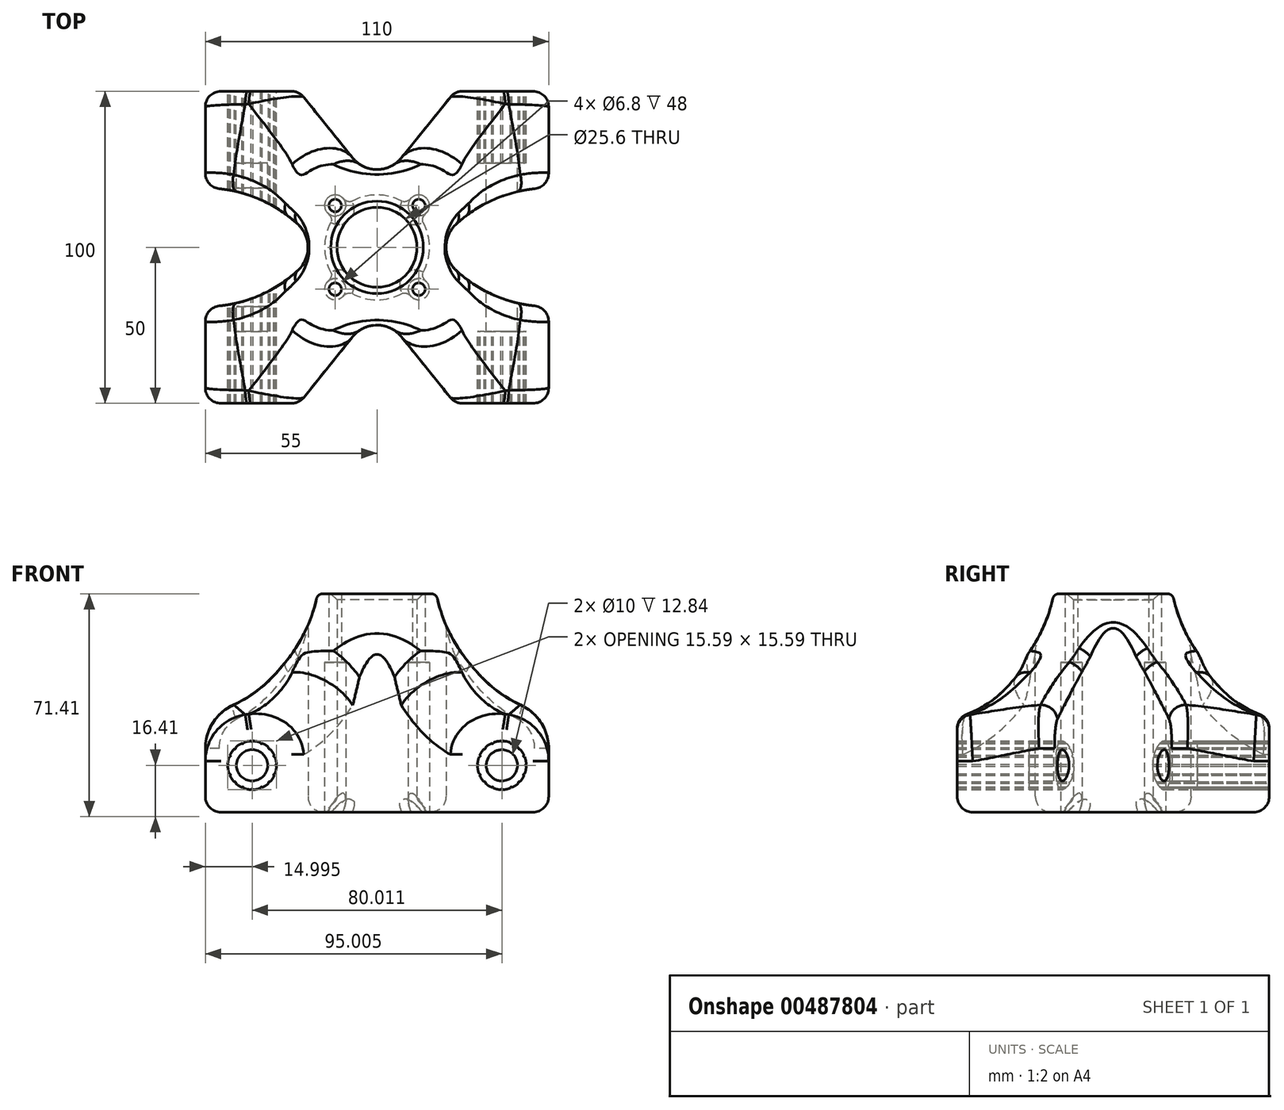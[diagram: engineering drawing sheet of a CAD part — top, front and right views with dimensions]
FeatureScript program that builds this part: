
annotation { "Feature Type Name" : "Feature", "Feature Type Description" : "" }
export const myFeature = defineFeature(function(context is Context, id is Id, definition is map)
    precondition{}
    {
        {
            var Q0;
            Q0=qCreatedBy(makeId("Top.planeOp"),FACE);
            var sketch = newSketch(context, id + "F0", { "sketchPlane" : qUnion([Q0])});
            skCircle(sketch, "E0", {"center": v(13.4, 13.4) * mm, "radius": 2 * mm});
            skCircle(sketch, "E1", {"center": v(13.4, 13.4) * mm, "radius": 3.4 * mm});
            skCircle(sketch, "E2", {"center": v(0, 0) * mm, "radius": 12.8 * mm});
            skCircle(sketch, "E3.1.0", {"center": v(-13.4, 13.4) * mm, "radius": 3.4 * mm});
            skCircle(sketch, "E3.1.1", {"center": v(-13.4, 13.4) * mm, "radius": 2 * mm});
            skCircle(sketch, "E3.2.0", {"center": v(-13.4, -13.4) * mm, "radius": 3.4 * mm});
            skCircle(sketch, "E3.2.1", {"center": v(-13.4, -13.4) * mm, "radius": 2 * mm});
            skCircle(sketch, "E3.3.0", {"center": v(13.4, -13.4) * mm, "radius": 3.4 * mm});
            skCircle(sketch, "E3.3.1", {"center": v(13.4, -13.4) * mm, "radius": 2 * mm});
            skLineSegment(sketch, "E4.bottom", {"start": v(55, -50) * mm, "end": v(-55, -50) * mm});
            skLineSegment(sketch, "E4.top", {"start": v(55, 50) * mm, "end": v(-55, 50) * mm});
            skLineSegment(sketch, "E4.left", {"start": v(55, -50) * mm, "end": v(55, 50) * mm});
            skLineSegment(sketch, "E4.right", {"start": v(-55, -50) * mm, "end": v(-55, 50) * mm});
            skLineSegment(sketch, "E5.bottom", {"start": v(25, -50) * mm, "end": v(-25, -50) * mm});
            skLineSegment(sketch, "E5.top", {"start": v(25, 50) * mm, "end": v(-25, 50) * mm});
            skLineSegment(sketch, "E5.left", {"start": v(25, -50) * mm, "end": v(25, 50) * mm});
            skLineSegment(sketch, "E5.right", {"start": v(-25, -50) * mm, "end": v(-25, 50) * mm});
            skLineSegment(sketch, "E6.bottom", {"start": v(19, -19) * mm, "end": v(-19, -19) * mm});
            skLineSegment(sketch, "E6.top", {"start": v(19, 19) * mm, "end": v(-19, 19) * mm});
            skLineSegment(sketch, "E6.left", {"start": v(19, -19) * mm, "end": v(19, 19) * mm});
            skLineSegment(sketch, "E6.right", {"start": v(-19, -19) * mm, "end": v(-19, 19) * mm});
            skLineSegment(sketch, "E7.bottom", {"start": v(55, -19) * mm, "end": v(-55, -19) * mm});
            skLineSegment(sketch, "E7.top", {"start": v(55, 19) * mm, "end": v(-55, 19) * mm});
            skLineSegment(sketch, "E7.left", {"start": v(55, -19) * mm, "end": v(55, 19) * mm});
            skLineSegment(sketch, "E7.right", {"start": v(-55, -19) * mm, "end": v(-55, 19) * mm});
            skLineSegment(sketch, "E8", {"start": v(0, 19) * mm, "end": v(-25, 50) * mm});
            skLineSegment(sketch, "E9", {"start": v(25, 50) * mm, "end": v(0, 19) * mm});
            skLineSegment(sketch, "E10", {"start": v(-25, -19) * mm, "end": v(-19, 0) * mm});
            skLineSegment(sketch, "E11", {"start": v(-19, 0) * mm, "end": v(-25, 19) * mm});
            skLineSegment(sketch, "E12", {"start": v(19, 0) * mm, "end": v(25, 19) * mm});
            skLineSegment(sketch, "E13", {"start": v(19, 0) * mm, "end": v(25, -19) * mm});
            skLineSegment(sketch, "E14", {"start": v(-25, -50) * mm, "end": v(0, -19) * mm});
            skLineSegment(sketch, "E15", {"start": v(0, -19) * mm, "end": v(25, -50) * mm});
            skSolve(sketch);
        }
        {
            var Q0;
            Q0=qCreatedBy(makeId("Front.planeOp"),FACE);
            var sketch = newSketch(context, id + "F1", { "sketchPlane" : qUnion([Q0])});
            skPoint(sketch, "E16.middle", {"position": v(40, 15) * mm});
            skPoint(sketch, "E17.center", {"position": v(40, 10) * mm});
            skCircle(sketch, "E18", {"center": v(40, 15) * mm, "radius": 7.8 * mm});
            skCircle(sketch, "E19", {"center": v(40, 22.8) * mm, "radius": 0.3 * mm});
            skCircle(sketch, "E20.1.0", {"center": v(37.02, 22.2) * mm, "radius": 0.3 * mm});
            skCircle(sketch, "E20.2.0", {"center": v(34.49, 20.52) * mm, "radius": 0.3 * mm});
            skCircle(sketch, "E20.3.0", {"center": v(32.8, 17.98) * mm, "radius": 0.3 * mm});
            skCircle(sketch, "E20.4.0", {"center": v(32.2, 15) * mm, "radius": 0.3 * mm});
            skCircle(sketch, "E20.5.0", {"center": v(32.8, 12.02) * mm, "radius": 0.3 * mm});
            skCircle(sketch, "E20.6.0", {"center": v(34.49, 9.48) * mm, "radius": 0.3 * mm});
            skCircle(sketch, "E20.7.0", {"center": v(37.02, 7.8) * mm, "radius": 0.3 * mm});
            skCircle(sketch, "E20.8.0", {"center": v(40, 7.2) * mm, "radius": 0.3 * mm});
            skCircle(sketch, "E20.9.0", {"center": v(43, 7.8) * mm, "radius": 0.3 * mm});
            skCircle(sketch, "E21.1.10.0", {"center": v(45.52, 9.48) * mm, "radius": 0.3 * mm});
            skCircle(sketch, "E21.1.11.0", {"center": v(47.21, 12.02) * mm, "radius": 0.3 * mm});
            skCircle(sketch, "E21.1.12.0", {"center": v(47.8, 15) * mm, "radius": 0.3 * mm});
            skCircle(sketch, "E21.1.13.0", {"center": v(47.21, 17.98) * mm, "radius": 0.3 * mm});
            skCircle(sketch, "E21.1.14.0", {"center": v(45.52, 20.52) * mm, "radius": 0.3 * mm});
            skCircle(sketch, "E21.1.15.0", {"center": v(43, 22.2) * mm, "radius": 0.3 * mm});
            skCircle(sketch, "E22", {"center": v(40, 15) * mm, "radius": 5 * mm});
            skPoint(sketch, "E23.MirrorP", {"position": v(-40, 15) * mm});
            skPoint(sketch, "E24.MirrorP", {"position": v(-40, 10) * mm});
            skCircle(sketch, "E25.MirrorC", {"center": v(-45.52, 9.48) * mm, "radius": 0.3 * mm});
            skCircle(sketch, "E26.MirrorC", {"center": v(-32.8, 12.02) * mm, "radius": 0.3 * mm});
            skCircle(sketch, "E27.MirrorC", {"center": v(-37.02, 22.2) * mm, "radius": 0.3 * mm});
            skCircle(sketch, "E28.MirrorC", {"center": v(-43, 7.8) * mm, "radius": 0.3 * mm});
            skCircle(sketch, "E29.MirrorC", {"center": v(-32.8, 17.98) * mm, "radius": 0.3 * mm});
            skCircle(sketch, "E30.MirrorC", {"center": v(-47.21, 12.02) * mm, "radius": 0.3 * mm});
            skCircle(sketch, "E31.MirrorC", {"center": v(-47.21, 17.98) * mm, "radius": 0.3 * mm});
            skCircle(sketch, "E32.MirrorC", {"center": v(-45.52, 20.52) * mm, "radius": 0.3 * mm});
            skCircle(sketch, "E33.MirrorC", {"center": v(-34.49, 9.48) * mm, "radius": 0.3 * mm});
            skCircle(sketch, "E34.MirrorC", {"center": v(-40, 7.2) * mm, "radius": 0.3 * mm});
            skCircle(sketch, "E35.MirrorC", {"center": v(-37.02, 7.8) * mm, "radius": 0.3 * mm});
            skCircle(sketch, "E36.MirrorC", {"center": v(-32.2, 15) * mm, "radius": 0.3 * mm});
            skCircle(sketch, "E37.MirrorC", {"center": v(-34.49, 20.52) * mm, "radius": 0.3 * mm});
            skCircle(sketch, "E38.MirrorC", {"center": v(-40, 22.8) * mm, "radius": 0.3 * mm});
            skCircle(sketch, "E39.MirrorC", {"center": v(-43, 22.2) * mm, "radius": 0.3 * mm});
            skCircle(sketch, "E40.MirrorC", {"center": v(-47.8, 15) * mm, "radius": 0.3 * mm});
            skCircle(sketch, "E41.MirrorC", {"center": v(-40, 15) * mm, "radius": 5 * mm});
            skCircle(sketch, "E42.MirrorC", {"center": v(-40, 15) * mm, "radius": 7.8 * mm});
            skLineSegment(sketch, "E43", {"start": v(-40, 15) * mm, "end": v(40, 15) * mm, "construction": true});
            skSolve(sketch);
        }
        {
            var Q0;
            Q0=makeQuery(id+"F0.imprint","IMPRINT",FACE,{"disambiguationData":[TD([[makeQuery(id+"F0.imprint","IMPRINT",EDGE,{"derivedFrom":sQuery(id+"F0.wireOp",EDGE,"E1")}),-1.0]])]});
            var Q1;
            Q1=makeQuery(id+"F0.imprint","IMPRINT",FACE,{"disambiguationData":[TD([[makeQuery(id+"F0.imprint","IMPRINT",EDGE,{"derivedFrom":sQuery(id+"F0.wireOp",EDGE,"E3.2.0")}),1.0]])]});
            var Q2;
            Q2=makeQuery(id+"F0.imprint","IMPRINT",FACE,{"disambiguationData":[TD([[makeQuery(id+"F0.imprint","IMPRINT",EDGE,{"derivedFrom":sQuery(id+"F0.wireOp",EDGE,"E3.3.0")}),1.0]])]});
            var Q3;
            Q3=makeQuery(id+"F0.imprint","IMPRINT",FACE,{"disambiguationData":[TD([[makeQuery(id+"F0.imprint","IMPRINT",EDGE,{"derivedFrom":sQuery(id+"F0.wireOp",EDGE,"E0")}),-1.0]])]});
            var Q4;
            Q4=makeQuery(id+"F0.imprint","IMPRINT",FACE,{"disambiguationData":[TD([[makeQuery(id+"F0.imprint","IMPRINT",EDGE,{"derivedFrom":sQuery(id+"F0.wireOp",EDGE,"E3.1.0")}),1.0]])]});
            extrude(context, id + "F2", {"entities" : qUnion([Q0, Q1, Q2, Q3, Q4]), "depth" : 70 * mm, "offsetDistance" : 25 * mm});
        }
        {
            var Q0;
            Q0=makeQuery(id+"F0.imprint","IMPRINT",FACE,{"disambiguationData":[TD([[makeQuery(id+"F0.imprint","IMPRINT",EDGE,{"derivedFrom":sQuery(id+"F0.wireOp",EDGE,"E3.2.0")}),1.0]])]});
            var Q1;
            Q1=makeQuery(id+"F0.imprint","IMPRINT",FACE,{"disambiguationData":[TD([[makeQuery(id+"F0.imprint","IMPRINT",EDGE,{"derivedFrom":sQuery(id+"F0.wireOp",EDGE,"E3.3.0")}),1.0]])]});
            var Q2;
            Q2=makeQuery(id+"F0.imprint","IMPRINT",FACE,{"disambiguationData":[TD([[makeQuery(id+"F0.imprint","IMPRINT",EDGE,{"derivedFrom":sQuery(id+"F0.wireOp",EDGE,"E0")}),-1.0]])]});
            var Q3;
            Q3=makeQuery(id+"F0.imprint","IMPRINT",FACE,{"disambiguationData":[TD([[makeQuery(id+"F0.imprint","IMPRINT",EDGE,{"derivedFrom":sQuery(id+"F0.wireOp",EDGE,"E3.1.0")}),1.0]])]});
            extrude(context, id + "F3", {"entities" : qUnion([Q0, Q1, Q2, Q3]), "operationType" : NewBodyOperationType.REMOVE, "depth" : (70 - 22) * mm, "offsetDistance" : 25 * mm});
        }
        {
            var Q0;
            {var subQ0=sQuery(id+"F0.wireOp",EDGE,"E14");Q0=makeQuery(id+"F0.imprint","IMPRINT",FACE,{"disambiguationData":[TD([[makeQuery(id+"F0.imprint","IMPRINT",EDGE,{"derivedFrom":subQ0}),1.0]])]});}
            var Q1;
            {var subQ3=sQuery(id+"F0.wireOp",EDGE,"E10");Q1=makeQuery(id+"F0.imprint","IMPRINT",FACE,{"disambiguationData":[TD([[makeQuery(id+"F0.imprint","IMPRINT",EDGE,{"derivedFrom":subQ3}),-1.0]])]});}
            var Q2;
            {var subQ3=sQuery(id+"F0.wireOp",EDGE,"E11");Q2=makeQuery(id+"F0.imprint","IMPRINT",FACE,{"disambiguationData":[TD([[makeQuery(id+"F0.imprint","IMPRINT",EDGE,{"derivedFrom":subQ3}),-1.0]])]});}
            var Q3;
            {var subQ0=sQuery(id+"F0.wireOp",EDGE,"E8");Q3=makeQuery(id+"F0.imprint","IMPRINT",FACE,{"disambiguationData":[TD([[makeQuery(id+"F0.imprint","IMPRINT",EDGE,{"derivedFrom":subQ0}),1.0]])]});}
            var Q4;
            {var subQ0=sQuery(id+"F0.wireOp",EDGE,"E9");Q4=makeQuery(id+"F0.imprint","IMPRINT",FACE,{"disambiguationData":[TD([[makeQuery(id+"F0.imprint","IMPRINT",EDGE,{"derivedFrom":subQ0}),1.0]])]});}
            var Q5;
            {var subQ3=sQuery(id+"F0.wireOp",EDGE,"E13");Q5=makeQuery(id+"F0.imprint","IMPRINT",FACE,{"disambiguationData":[TD([[makeQuery(id+"F0.imprint","IMPRINT",EDGE,{"derivedFrom":subQ3}),-1.0]])]});}
            var Q6;
            {var subQ3=sQuery(id+"F0.wireOp",EDGE,"E12");Q6=makeQuery(id+"F0.imprint","IMPRINT",FACE,{"disambiguationData":[TD([[makeQuery(id+"F0.imprint","IMPRINT",EDGE,{"derivedFrom":subQ3}),1.0]])]});}
            var Q7;
            {var subQ0=sQuery(id+"F0.wireOp",EDGE,"E15");Q7=makeQuery(id+"F0.imprint","IMPRINT",FACE,{"disambiguationData":[TD([[makeQuery(id+"F0.imprint","IMPRINT",EDGE,{"derivedFrom":subQ0}),1.0]])]});}
            var Q8;
            {var subQ0=sQuery(id+"F0.wireOp",EDGE,"E4.right");var subQ1=sQuery(id+"F0.wireOp",EDGE,"E4.bottom");var subQ2=makeQuery(id+"F0.imprint","INTERSECT",VERTEX,{"derivedFrom":[subQ1,subQ0]});Q8=makeQuery(id+"F0.imprint","IMPRINT",FACE,{"disambiguationData":[TD([[makeQuery(id+"F0.imprint","IMPRINT",EDGE,{"disambiguationData":[TD([[subQ2,-1.0]])],"derivedFrom":subQ0}),-1.0]])]});}
            var Q9;
            {var subQ0=sQuery(id+"F0.wireOp",EDGE,"E4.left");var subQ1=sQuery(id+"F0.wireOp",EDGE,"E4.bottom");var subQ2=makeQuery(id+"F0.imprint","INTERSECT",VERTEX,{"derivedFrom":[subQ1,subQ0]});Q9=makeQuery(id+"F0.imprint","IMPRINT",FACE,{"disambiguationData":[TD([[makeQuery(id+"F0.imprint","IMPRINT",EDGE,{"disambiguationData":[TD([[subQ2,-1.0]])],"derivedFrom":subQ0}),1.0]])]});}
            var Q10;
            {var subQ0=sQuery(id+"F0.wireOp",EDGE,"E4.left");var subQ1=sQuery(id+"F0.wireOp",EDGE,"E4.top");var subQ2=makeQuery(id+"F0.imprint","INTERSECT",VERTEX,{"derivedFrom":[subQ1,subQ0]});Q10=makeQuery(id+"F0.imprint","IMPRINT",FACE,{"disambiguationData":[TD([[makeQuery(id+"F0.imprint","IMPRINT",EDGE,{"disambiguationData":[TD([[subQ2,1.0]])],"derivedFrom":subQ0}),1.0]])]});}
            var Q11;
            {var subQ0=sQuery(id+"F0.wireOp",EDGE,"E4.right");var subQ1=sQuery(id+"F0.wireOp",EDGE,"E4.top");var subQ2=makeQuery(id+"F0.imprint","INTERSECT",VERTEX,{"derivedFrom":[subQ1,subQ0]});Q11=makeQuery(id+"F0.imprint","IMPRINT",FACE,{"disambiguationData":[TD([[makeQuery(id+"F0.imprint","IMPRINT",EDGE,{"disambiguationData":[TD([[subQ2,1.0]])],"derivedFrom":subQ0}),-1.0]])]});}
            extrude(context, id + "F4", {"entities" : qUnion([Q0, Q1, Q2, Q3, Q4, Q5, Q6, Q7, Q8, Q9, Q10, Q11]), "operationType" : NewBodyOperationType.ADD, "depth" : 30 * mm, "offsetDistance" : 25 * mm});
        }
        {
            var Q0;
            Q0=makeQuery(id+"F1.imprint","IMPRINT",FACE,{"disambiguationData":[TD([[makeQuery(id+"F1.imprint","IMPRINT",EDGE,{"derivedFrom":sQuery(id+"F1.wireOp",EDGE,"E41.MirrorC")}),-1.0]])]});
            var Q1;
            Q1=makeQuery(id+"F1.imprint","IMPRINT",FACE,{"disambiguationData":[TD([[makeQuery(id+"F1.imprint","IMPRINT",EDGE,{"derivedFrom":sQuery(id+"F1.wireOp",EDGE,"E22")}),1.0]])]});
            var Q2;
            Q2=makeQuery(id+"F1.imprint","IMPRINT",FACE,{"disambiguationData":[TD([[makeQuery(id+"F1.imprint","IMPRINT",EDGE,{"derivedFrom":sQuery(id+"F1.wireOp",EDGE,"E22")}),-1.0]])]});
            var Q3;
            Q3=makeQuery(id+"F1.imprint","IMPRINT",FACE,{"disambiguationData":[TD([[makeQuery(id+"F1.imprint","IMPRINT",EDGE,{"derivedFrom":sQuery(id+"F1.wireOp",EDGE,"E41.MirrorC")}),1.0]])]});
            extrude(context, id + "F5", {"entities" : qUnion([Q0, Q1, Q2, Q3]), "operationType" : NewBodyOperationType.REMOVE, "endBound" : BoundingType.SYMMETRIC, "depth" : 200 * mm});
        }
        {
            var Q0;
            Q0=makeQuery(id+"F1.imprint","IMPRINT",FACE,{"disambiguationData":[TD([[makeQuery(id+"F1.imprint","IMPRINT",EDGE,{"derivedFrom":sQuery(id+"F1.wireOp",EDGE,"E22")}),-1.0]])]});
            var Q1;
            Q1=makeQuery(id+"F1.imprint","IMPRINT",FACE,{"disambiguationData":[TD([[makeQuery(id+"F1.imprint","IMPRINT",EDGE,{"derivedFrom":sQuery(id+"F1.wireOp",EDGE,"E41.MirrorC")}),1.0]])]});
            extrude(context, id + "F6", {"entities" : qUnion([Q0, Q1]), "operationType" : NewBodyOperationType.ADD, "endBound" : BoundingType.SYMMETRIC, "depth" : 54 * mm, "offsetDistance" : 25 * mm});
        }
        {
            var Q0;
            Q0=makeQuery(id+"F1.imprint","IMPRINT",FACE,{"disambiguationData":[TD([[makeQuery(id+"F1.imprint","IMPRINT",EDGE,{"derivedFrom":sQuery(id+"F1.wireOp",EDGE,"E22")}),-1.0]])]});
            var Q1;
            Q1=makeQuery(id+"F1.imprint","IMPRINT",FACE,{"disambiguationData":[TD([[makeQuery(id+"F1.imprint","IMPRINT",EDGE,{"derivedFrom":sQuery(id+"F1.wireOp",EDGE,"E41.MirrorC")}),1.0]])]});
            extrude(context, id + "F7", {"entities" : qUnion([Q0, Q1]), "operationType" : NewBodyOperationType.REMOVE, "endBound" : BoundingType.SYMMETRIC, "oppositeDirection" : true, "depth" : 38 * mm});
        }
        {
            var Q0;
            Q0=makeQuery(id+"F4.opExtrude","SWEPT_EDGE",EDGE,{"disambiguationData":[OSD([sQuery(id+"F0.wireOp",EDGE,"E5.left"),sQuery(id+"F0.wireOp",EDGE,"E7.top"),sQuery(id+"F0.wireOp",EDGE,"E12")])]});
            var Q1;
            Q1=makeQuery(id+"F4.opExtrude","SWEPT_EDGE",EDGE,{"disambiguationData":[OSD([sQuery(id+"F0.wireOp",EDGE,"E5.left"),sQuery(id+"F0.wireOp",EDGE,"E7.bottom"),sQuery(id+"F0.wireOp",EDGE,"E13")])]});
            var Q2;
            Q2=makeQuery(id+"F4.opExtrude","SWEPT_EDGE",EDGE,{"disambiguationData":[OSD([sQuery(id+"F0.wireOp",EDGE,"E5.right"),sQuery(id+"F0.wireOp",EDGE,"E7.bottom"),sQuery(id+"F0.wireOp",EDGE,"E10")])]});
            var Q3;
            Q3=makeQuery(id+"F4.opExtrude","SWEPT_EDGE",EDGE,{"disambiguationData":[OSD([sQuery(id+"F0.wireOp",EDGE,"E5.right"),sQuery(id+"F0.wireOp",EDGE,"E7.top"),sQuery(id+"F0.wireOp",EDGE,"E11")])]});
            fillet(context, id + "F8", {"entities" : qUnion([Q0, Q1, Q2, Q3]), "radius" : 43.5 * mm, "tangentPropagation" : true, "allowEdgeOverflow" : false});
        }
        {
            var Q0;
            Q0=makeQuery(id+"F2.opExtrude","SWEPT_EDGE",EDGE,{"disambiguationData":[OSD([sQuery(id+"F0.wireOp",EDGE,"E6.left"),sQuery(id+"F0.wireOp",EDGE,"E7.bottom")])]});
            var Q1;
            Q1=makeQuery(id+"F2.opExtrude","SWEPT_EDGE",EDGE,{"disambiguationData":[OSD([sQuery(id+"F0.wireOp",EDGE,"E6.left"),sQuery(id+"F0.wireOp",EDGE,"E7.top")])]});
            var Q2;
            Q2=makeQuery(id+"F2.opExtrude","SWEPT_EDGE",EDGE,{"disambiguationData":[OSD([sQuery(id+"F0.wireOp",EDGE,"E6.right"),sQuery(id+"F0.wireOp",EDGE,"E7.top")])]});
            var Q3;
            Q3=makeQuery(id+"F2.opExtrude","SWEPT_EDGE",EDGE,{"disambiguationData":[OSD([sQuery(id+"F0.wireOp",EDGE,"E6.right"),sQuery(id+"F0.wireOp",EDGE,"E7.bottom")])]});
            fillet(context, id + "F9", {"entities" : qUnion([Q0, Q1, Q2, Q3]), "radius" : 5 * mm, "tangentPropagation" : true, "allowEdgeOverflow" : false});
        }
        {
            var Q0;
            {var subQ0=sQuery(id+"F0.wireOp",EDGE,"E15");var subQ1=sQuery(id+"F0.wireOp",EDGE,"E14");var subQ2=sQuery(id+"F0.wireOp",EDGE,"E7.bottom");Q0=makeQuery(id+"F4.boolean.opBoolean","MERGE",EDGE,{"derivedFrom":[makeQuery(id+"F4.opExtrude","SWEPT_EDGE",EDGE,{"disambiguationData":[OSD([subQ2,subQ1,subQ0]),OD(0.0)]}),makeQuery(id+"F4.opExtrude","SWEPT_EDGE",EDGE,{"disambiguationData":[OSD([subQ2,subQ1,subQ0]),OD(1.0)]})]});}
            var Q1;
            {var subQ0=sQuery(id+"F0.wireOp",EDGE,"E9");var subQ1=sQuery(id+"F0.wireOp",EDGE,"E8");var subQ2=sQuery(id+"F0.wireOp",EDGE,"E7.top");Q1=makeQuery(id+"F4.boolean.opBoolean","MERGE",EDGE,{"derivedFrom":[makeQuery(id+"F4.opExtrude","SWEPT_EDGE",EDGE,{"disambiguationData":[OSD([subQ2,subQ1,subQ0]),OD(0.0)]}),makeQuery(id+"F4.opExtrude","SWEPT_EDGE",EDGE,{"disambiguationData":[OSD([subQ2,subQ1,subQ0]),OD(1.0)]})]});}
            var Q2;
            {var subQ0=sQuery(id+"F0.wireOp",EDGE,"E5.left");Q2=makeQuery(id+"F8.opFillet","BLEND_EDGE",EDGE,{"blendedFrom":[makeQuery(id+"F4.opExtrude","SWEPT_EDGE",EDGE,{"disambiguationData":[OSD([subQ0,sQuery(id+"F0.wireOp",EDGE,"E7.top"),sQuery(id+"F0.wireOp",EDGE,"E12")])]}),makeQuery(id+"F4.opExtrude","SWEPT_EDGE",EDGE,{"disambiguationData":[OSD([subQ0,sQuery(id+"F0.wireOp",EDGE,"E7.bottom"),sQuery(id+"F0.wireOp",EDGE,"E13")])]})],"blendedInto":[]});}
            var Q3;
            {var subQ0=sQuery(id+"F0.wireOp",EDGE,"E5.right");Q3=makeQuery(id+"F8.opFillet","BLEND_EDGE",EDGE,{"blendedFrom":[makeQuery(id+"F4.opExtrude","SWEPT_EDGE",EDGE,{"disambiguationData":[OSD([subQ0,sQuery(id+"F0.wireOp",EDGE,"E7.bottom"),sQuery(id+"F0.wireOp",EDGE,"E10")])]}),makeQuery(id+"F4.opExtrude","SWEPT_EDGE",EDGE,{"disambiguationData":[OSD([subQ0,sQuery(id+"F0.wireOp",EDGE,"E7.top"),sQuery(id+"F0.wireOp",EDGE,"E11")])]})],"blendedInto":[]});}
            fillet(context, id + "F10", {"entities" : qUnion([Q0, Q1, Q2, Q3]), "radius" : 10 * mm, "tangentPropagation" : true, "allowEdgeOverflow" : false});
        }
        {
            var Q0;
            {var subQ0=sQuery(id+"F0.wireOp",EDGE,"E7.top");var subQ1=sQuery(id+"F0.wireOp",EDGE,"E6.right");Q0=makeQuery(id+"F9.opFillet","BLEND_EDGE",EDGE,{"blendedFrom":[makeQuery(id+"F2.opExtrude","SWEPT_EDGE",EDGE,{"disambiguationData":[OSD([subQ1,subQ0])]}),makeQuery(id+"F4.opExtrude","CAP_FACE",FACE,{"disambiguationData":[OSD([sQuery(id+"F0.wireOp",EDGE,"E4.top"),sQuery(id+"F0.wireOp",EDGE,"E4.right"),subQ1,subQ0,sQuery(id+"F0.wireOp",EDGE,"E8"),sQuery(id+"F0.wireOp",EDGE,"E11")])],"isStart":false})],"blendedInto":[makeQuery(id+"F4.opExtrude","CAP_FACE",FACE,{"disambiguationData":[OSD([sQuery(id+"F0.wireOp",EDGE,"E4.top"),sQuery(id+"F0.wireOp",EDGE,"E4.right"),subQ1,subQ0,sQuery(id+"F0.wireOp",EDGE,"E8"),sQuery(id+"F0.wireOp",EDGE,"E11")])],"isStart":false})]});}
            fillet(context, id + "F11", {"entities" : qUnion([Q0]), "radius" : 49.5 * mm, "tangentPropagation" : true, "allowEdgeOverflow" : false});
        }
        {
            var Q0;
            {var subQ0=sQuery(id+"F0.wireOp",EDGE,"E4.left");var subQ1=sQuery(id+"F0.wireOp",EDGE,"E4.bottom");var subQ2=sQuery(id+"F0.wireOp",EDGE,"E7.bottom");var subQ3=sQuery(id+"F0.wireOp",EDGE,"E6.left");Q0=makeQuery(id+"F11.opFillet","BLEND_EDGE",EDGE,{"blendedFrom":[makeQuery(id+"F9.opFillet","BLEND_EDGE",EDGE,{"blendedFrom":[makeQuery(id+"F2.opExtrude","SWEPT_EDGE",EDGE,{"disambiguationData":[OSD([subQ3,subQ2])]}),makeQuery(id+"F4.opExtrude","CAP_FACE",FACE,{"disambiguationData":[OSD([subQ1,subQ0,subQ3,subQ2,sQuery(id+"F0.wireOp",EDGE,"E13"),sQuery(id+"F0.wireOp",EDGE,"E15")])],"isStart":false})],"blendedInto":[makeQuery(id+"F4.opExtrude","CAP_FACE",FACE,{"disambiguationData":[OSD([subQ1,subQ0,subQ3,subQ2,sQuery(id+"F0.wireOp",EDGE,"E13"),sQuery(id+"F0.wireOp",EDGE,"E15")])],"isStart":false})]}),makeQuery(id+"F4.opExtrude","SWEPT_FACE",FACE,{"disambiguationData":[OSD([subQ0]),TDD([makeQuery(id+"F0.imprint","IMPRINT",EDGE,{"disambiguationData":[TD([[makeQuery(id+"F0.imprint","INTERSECT",VERTEX,{"derivedFrom":[subQ1,subQ0]}),-1.0]])],"derivedFrom":subQ0})])]})],"blendedInto":[makeQuery(id+"F4.opExtrude","SWEPT_FACE",FACE,{"disambiguationData":[OSD([subQ0]),TDD([makeQuery(id+"F0.imprint","IMPRINT",EDGE,{"disambiguationData":[TD([[makeQuery(id+"F0.imprint","INTERSECT",VERTEX,{"derivedFrom":[subQ1,subQ0]}),-1.0]])],"derivedFrom":subQ0})])]})]});}
            var Q1;
            {var subQ0=sQuery(id+"F0.wireOp",EDGE,"E4.left");var subQ1=sQuery(id+"F0.wireOp",EDGE,"E4.top");var subQ2=sQuery(id+"F0.wireOp",EDGE,"E7.top");var subQ3=sQuery(id+"F0.wireOp",EDGE,"E6.left");Q1=makeQuery(id+"F11.opFillet","BLEND_EDGE",EDGE,{"blendedFrom":[makeQuery(id+"F9.opFillet","BLEND_EDGE",EDGE,{"blendedFrom":[makeQuery(id+"F2.opExtrude","SWEPT_EDGE",EDGE,{"disambiguationData":[OSD([subQ3,subQ2])]}),makeQuery(id+"F4.opExtrude","CAP_FACE",FACE,{"disambiguationData":[OSD([subQ1,subQ0,subQ3,subQ2,sQuery(id+"F0.wireOp",EDGE,"E9"),sQuery(id+"F0.wireOp",EDGE,"E12")])],"isStart":false})],"blendedInto":[makeQuery(id+"F4.opExtrude","CAP_FACE",FACE,{"disambiguationData":[OSD([subQ1,subQ0,subQ3,subQ2,sQuery(id+"F0.wireOp",EDGE,"E9"),sQuery(id+"F0.wireOp",EDGE,"E12")])],"isStart":false})]}),makeQuery(id+"F4.opExtrude","SWEPT_FACE",FACE,{"disambiguationData":[OSD([subQ0]),TDD([makeQuery(id+"F0.imprint","IMPRINT",EDGE,{"disambiguationData":[TD([[makeQuery(id+"F0.imprint","INTERSECT",VERTEX,{"derivedFrom":[subQ1,subQ0]}),1.0]])],"derivedFrom":subQ0})])]})],"blendedInto":[makeQuery(id+"F4.opExtrude","SWEPT_FACE",FACE,{"disambiguationData":[OSD([subQ0]),TDD([makeQuery(id+"F0.imprint","IMPRINT",EDGE,{"disambiguationData":[TD([[makeQuery(id+"F0.imprint","INTERSECT",VERTEX,{"derivedFrom":[subQ1,subQ0]}),1.0]])],"derivedFrom":subQ0})])]})]});}
            var Q2;
            {var subQ0=sQuery(id+"F0.wireOp",EDGE,"E4.right");var subQ1=sQuery(id+"F0.wireOp",EDGE,"E4.top");var subQ2=sQuery(id+"F0.wireOp",EDGE,"E7.top");var subQ3=sQuery(id+"F0.wireOp",EDGE,"E6.right");Q2=makeQuery(id+"F11.opFillet","BLEND_EDGE",EDGE,{"blendedFrom":[makeQuery(id+"F9.opFillet","BLEND_EDGE",EDGE,{"blendedFrom":[makeQuery(id+"F2.opExtrude","SWEPT_EDGE",EDGE,{"disambiguationData":[OSD([subQ3,subQ2])]}),makeQuery(id+"F4.opExtrude","CAP_FACE",FACE,{"disambiguationData":[OSD([subQ1,subQ0,subQ3,subQ2,sQuery(id+"F0.wireOp",EDGE,"E8"),sQuery(id+"F0.wireOp",EDGE,"E11")])],"isStart":false})],"blendedInto":[makeQuery(id+"F4.opExtrude","CAP_FACE",FACE,{"disambiguationData":[OSD([subQ1,subQ0,subQ3,subQ2,sQuery(id+"F0.wireOp",EDGE,"E8"),sQuery(id+"F0.wireOp",EDGE,"E11")])],"isStart":false})]}),makeQuery(id+"F4.opExtrude","SWEPT_FACE",FACE,{"disambiguationData":[OSD([subQ0]),TDD([makeQuery(id+"F0.imprint","IMPRINT",EDGE,{"disambiguationData":[TD([[makeQuery(id+"F0.imprint","INTERSECT",VERTEX,{"derivedFrom":[subQ1,subQ0]}),1.0]])],"derivedFrom":subQ0})])]})],"blendedInto":[makeQuery(id+"F4.opExtrude","SWEPT_FACE",FACE,{"disambiguationData":[OSD([subQ0]),TDD([makeQuery(id+"F0.imprint","IMPRINT",EDGE,{"disambiguationData":[TD([[makeQuery(id+"F0.imprint","INTERSECT",VERTEX,{"derivedFrom":[subQ1,subQ0]}),1.0]])],"derivedFrom":subQ0})])]})]});}
            var Q3;
            {var subQ0=sQuery(id+"F0.wireOp",EDGE,"E4.right");var subQ1=sQuery(id+"F0.wireOp",EDGE,"E4.bottom");var subQ2=sQuery(id+"F0.wireOp",EDGE,"E7.bottom");var subQ3=sQuery(id+"F0.wireOp",EDGE,"E6.right");Q3=makeQuery(id+"F11.opFillet","BLEND_EDGE",EDGE,{"blendedFrom":[makeQuery(id+"F9.opFillet","BLEND_EDGE",EDGE,{"blendedFrom":[makeQuery(id+"F2.opExtrude","SWEPT_EDGE",EDGE,{"disambiguationData":[OSD([subQ3,subQ2])]}),makeQuery(id+"F4.opExtrude","CAP_FACE",FACE,{"disambiguationData":[OSD([subQ1,subQ0,subQ3,subQ2,sQuery(id+"F0.wireOp",EDGE,"E10"),sQuery(id+"F0.wireOp",EDGE,"E14")])],"isStart":false})],"blendedInto":[makeQuery(id+"F4.opExtrude","CAP_FACE",FACE,{"disambiguationData":[OSD([subQ1,subQ0,subQ3,subQ2,sQuery(id+"F0.wireOp",EDGE,"E10"),sQuery(id+"F0.wireOp",EDGE,"E14")])],"isStart":false})]}),makeQuery(id+"F4.opExtrude","SWEPT_FACE",FACE,{"disambiguationData":[OSD([subQ0]),TDD([makeQuery(id+"F0.imprint","IMPRINT",EDGE,{"disambiguationData":[TD([[makeQuery(id+"F0.imprint","INTERSECT",VERTEX,{"derivedFrom":[subQ1,subQ0]}),-1.0]])],"derivedFrom":subQ0})])]})],"blendedInto":[makeQuery(id+"F4.opExtrude","SWEPT_FACE",FACE,{"disambiguationData":[OSD([subQ0]),TDD([makeQuery(id+"F0.imprint","IMPRINT",EDGE,{"disambiguationData":[TD([[makeQuery(id+"F0.imprint","INTERSECT",VERTEX,{"derivedFrom":[subQ1,subQ0]}),-1.0]])],"derivedFrom":subQ0})])]})]});}
            var Q4;
            {var subQ0=sQuery(id+"F0.wireOp",EDGE,"E9");var subQ1=sQuery(id+"F0.wireOp",EDGE,"E7.top");var subQ2=sQuery(id+"F0.wireOp",EDGE,"E6.left");Q4=makeQuery(id+"F11.opFillet","BLEND_EDGE",EDGE,{"blendedFrom":[makeQuery(id+"F9.opFillet","BLEND_EDGE",EDGE,{"blendedFrom":[makeQuery(id+"F2.opExtrude","SWEPT_EDGE",EDGE,{"disambiguationData":[OSD([subQ2,subQ1])]}),makeQuery(id+"F4.opExtrude","CAP_FACE",FACE,{"disambiguationData":[OSD([sQuery(id+"F0.wireOp",EDGE,"E4.top"),sQuery(id+"F0.wireOp",EDGE,"E4.left"),subQ2,subQ1,subQ0,sQuery(id+"F0.wireOp",EDGE,"E12")])],"isStart":false})],"blendedInto":[makeQuery(id+"F4.opExtrude","CAP_FACE",FACE,{"disambiguationData":[OSD([sQuery(id+"F0.wireOp",EDGE,"E4.top"),sQuery(id+"F0.wireOp",EDGE,"E4.left"),subQ2,subQ1,subQ0,sQuery(id+"F0.wireOp",EDGE,"E12")])],"isStart":false})]}),makeQuery(id+"F10.opFillet","BLEND_FACE",FACE,{"disambiguationData":[OSD([subQ1,sQuery(id+"F0.wireOp",EDGE,"E8"),subQ0])]})],"blendedInto":[makeQuery(id+"F10.opFillet","BLEND_FACE",FACE,{"disambiguationData":[OSD([subQ1,sQuery(id+"F0.wireOp",EDGE,"E8"),subQ0])]})]});}
            var Q5;
            {var subQ0=sQuery(id+"F0.wireOp",EDGE,"E14");var subQ1=sQuery(id+"F0.wireOp",EDGE,"E7.bottom");var subQ2=sQuery(id+"F0.wireOp",EDGE,"E6.right");Q5=makeQuery(id+"F11.opFillet","BLEND_EDGE",EDGE,{"blendedFrom":[makeQuery(id+"F9.opFillet","BLEND_EDGE",EDGE,{"blendedFrom":[makeQuery(id+"F2.opExtrude","SWEPT_EDGE",EDGE,{"disambiguationData":[OSD([subQ2,subQ1])]}),makeQuery(id+"F4.opExtrude","CAP_FACE",FACE,{"disambiguationData":[OSD([sQuery(id+"F0.wireOp",EDGE,"E4.bottom"),sQuery(id+"F0.wireOp",EDGE,"E4.right"),subQ2,subQ1,sQuery(id+"F0.wireOp",EDGE,"E10"),subQ0])],"isStart":false})],"blendedInto":[makeQuery(id+"F4.opExtrude","CAP_FACE",FACE,{"disambiguationData":[OSD([sQuery(id+"F0.wireOp",EDGE,"E4.bottom"),sQuery(id+"F0.wireOp",EDGE,"E4.right"),subQ2,subQ1,sQuery(id+"F0.wireOp",EDGE,"E10"),subQ0])],"isStart":false})]}),makeQuery(id+"F10.opFillet","BLEND_FACE",FACE,{"disambiguationData":[OSD([subQ1,subQ0,sQuery(id+"F0.wireOp",EDGE,"E15")])]})],"blendedInto":[makeQuery(id+"F10.opFillet","BLEND_FACE",FACE,{"disambiguationData":[OSD([subQ1,subQ0,sQuery(id+"F0.wireOp",EDGE,"E15")])]})]});}
            fillet(context, id + "F12", {"entities" : qUnion([Q0, Q1, Q2, Q3, Q4, Q5]), "radius" : 15 * mm, "tangentPropagation" : true, "allowEdgeOverflow" : false});
        }
        {
            var Q0;
            {var subQ0=sQuery(id+"F0.wireOp",EDGE,"E13");var subQ1=sQuery(id+"F0.wireOp",EDGE,"E7.bottom");var subQ2=sQuery(id+"F0.wireOp",EDGE,"E6.left");Q0=makeQuery(id+"F11.opFillet","BLEND_EDGE",EDGE,{"blendedFrom":[makeQuery(id+"F9.opFillet","BLEND_EDGE",EDGE,{"blendedFrom":[makeQuery(id+"F2.opExtrude","SWEPT_EDGE",EDGE,{"disambiguationData":[OSD([subQ2,subQ1])]}),makeQuery(id+"F4.opExtrude","CAP_FACE",FACE,{"disambiguationData":[OSD([sQuery(id+"F0.wireOp",EDGE,"E4.bottom"),sQuery(id+"F0.wireOp",EDGE,"E4.left"),subQ2,subQ1,subQ0,sQuery(id+"F0.wireOp",EDGE,"E15")])],"isStart":false})],"blendedInto":[makeQuery(id+"F4.opExtrude","CAP_FACE",FACE,{"disambiguationData":[OSD([sQuery(id+"F0.wireOp",EDGE,"E4.bottom"),sQuery(id+"F0.wireOp",EDGE,"E4.left"),subQ2,subQ1,subQ0,sQuery(id+"F0.wireOp",EDGE,"E15")])],"isStart":false})]}),makeQuery(id+"F10.opFillet","BLEND_FACE",FACE,{"disambiguationData":[OSD([sQuery(id+"F0.wireOp",EDGE,"E5.left"),subQ1,sQuery(id+"F0.wireOp",EDGE,"E7.top"),sQuery(id+"F0.wireOp",EDGE,"E12"),subQ0])]})],"blendedInto":[makeQuery(id+"F10.opFillet","BLEND_FACE",FACE,{"disambiguationData":[OSD([sQuery(id+"F0.wireOp",EDGE,"E5.left"),subQ1,sQuery(id+"F0.wireOp",EDGE,"E7.top"),sQuery(id+"F0.wireOp",EDGE,"E12"),subQ0])]})]});}
            var Q1;
            {var subQ0=sQuery(id+"F0.wireOp",EDGE,"E4.left");var subQ1=sQuery(id+"F0.wireOp",EDGE,"E4.top");var subQ2=makeQuery(id+"F0.imprint","INTERSECT",VERTEX,{"derivedFrom":[subQ1,subQ0]});var subQ3=sQuery(id+"F0.wireOp",EDGE,"E9");var subQ4=sQuery(id+"F0.wireOp",EDGE,"E7.top");var subQ5=sQuery(id+"F0.wireOp",EDGE,"E6.left");Q1=makeQuery(id+"F12.opFillet","BLEND_EDGE",EDGE,{"blendedFrom":[makeQuery(id+"F11.opFillet","BLEND_EDGE",EDGE,{"blendedFrom":[makeQuery(id+"F9.opFillet","BLEND_EDGE",EDGE,{"blendedFrom":[makeQuery(id+"F2.opExtrude","SWEPT_EDGE",EDGE,{"disambiguationData":[OSD([subQ5,subQ4])]}),makeQuery(id+"F4.opExtrude","CAP_FACE",FACE,{"disambiguationData":[OSD([subQ1,subQ0,subQ5,subQ4,subQ3,sQuery(id+"F0.wireOp",EDGE,"E12")])],"isStart":false})],"blendedInto":[makeQuery(id+"F4.opExtrude","CAP_FACE",FACE,{"disambiguationData":[OSD([subQ1,subQ0,subQ5,subQ4,subQ3,sQuery(id+"F0.wireOp",EDGE,"E12")])],"isStart":false})]}),makeQuery(id+"F4.opExtrude","SWEPT_FACE",FACE,{"disambiguationData":[OSD([subQ0]),TDD([makeQuery(id+"F0.imprint","IMPRINT",EDGE,{"disambiguationData":[TD([[subQ2,1.0]])],"derivedFrom":subQ0})])]})],"blendedInto":[makeQuery(id+"F4.opExtrude","SWEPT_FACE",FACE,{"disambiguationData":[OSD([subQ0]),TDD([makeQuery(id+"F0.imprint","IMPRINT",EDGE,{"disambiguationData":[TD([[subQ2,1.0]])],"derivedFrom":subQ0})])]})]}),makeQuery(id+"F4.opExtrude","SWEPT_FACE",FACE,{"disambiguationData":[OSD([subQ1]),TDD([makeQuery(id+"F0.imprint","IMPRINT",EDGE,{"disambiguationData":[TD([[subQ2,-1.0]])],"derivedFrom":subQ1})])]})],"blendedInto":[makeQuery(id+"F4.opExtrude","SWEPT_FACE",FACE,{"disambiguationData":[OSD([subQ1]),TDD([makeQuery(id+"F0.imprint","IMPRINT",EDGE,{"disambiguationData":[TD([[subQ2,-1.0]])],"derivedFrom":subQ1})])]})]});}
            var Q2;
            {var subQ0=sQuery(id+"F0.wireOp",EDGE,"E4.right");var subQ1=sQuery(id+"F0.wireOp",EDGE,"E4.top");var subQ2=makeQuery(id+"F0.imprint","INTERSECT",VERTEX,{"derivedFrom":[subQ1,subQ0]});var subQ3=sQuery(id+"F0.wireOp",EDGE,"E8");var subQ4=sQuery(id+"F0.wireOp",EDGE,"E7.top");var subQ5=sQuery(id+"F0.wireOp",EDGE,"E6.right");Q2=makeQuery(id+"F12.opFillet","BLEND_EDGE",EDGE,{"blendedFrom":[makeQuery(id+"F11.opFillet","BLEND_EDGE",EDGE,{"blendedFrom":[makeQuery(id+"F9.opFillet","BLEND_EDGE",EDGE,{"blendedFrom":[makeQuery(id+"F2.opExtrude","SWEPT_EDGE",EDGE,{"disambiguationData":[OSD([subQ5,subQ4])]}),makeQuery(id+"F4.opExtrude","CAP_FACE",FACE,{"disambiguationData":[OSD([subQ1,subQ0,subQ5,subQ4,subQ3,sQuery(id+"F0.wireOp",EDGE,"E11")])],"isStart":false})],"blendedInto":[makeQuery(id+"F4.opExtrude","CAP_FACE",FACE,{"disambiguationData":[OSD([subQ1,subQ0,subQ5,subQ4,subQ3,sQuery(id+"F0.wireOp",EDGE,"E11")])],"isStart":false})]}),makeQuery(id+"F4.opExtrude","SWEPT_FACE",FACE,{"disambiguationData":[OSD([subQ0]),TDD([makeQuery(id+"F0.imprint","IMPRINT",EDGE,{"disambiguationData":[TD([[subQ2,1.0]])],"derivedFrom":subQ0})])]})],"blendedInto":[makeQuery(id+"F4.opExtrude","SWEPT_FACE",FACE,{"disambiguationData":[OSD([subQ0]),TDD([makeQuery(id+"F0.imprint","IMPRINT",EDGE,{"disambiguationData":[TD([[subQ2,1.0]])],"derivedFrom":subQ0})])]})]}),makeQuery(id+"F4.opExtrude","SWEPT_FACE",FACE,{"disambiguationData":[OSD([subQ1]),TDD([makeQuery(id+"F0.imprint","IMPRINT",EDGE,{"disambiguationData":[TD([[subQ2,1.0]])],"derivedFrom":subQ1})])]})],"blendedInto":[makeQuery(id+"F4.opExtrude","SWEPT_FACE",FACE,{"disambiguationData":[OSD([subQ1]),TDD([makeQuery(id+"F0.imprint","IMPRINT",EDGE,{"disambiguationData":[TD([[subQ2,1.0]])],"derivedFrom":subQ1})])]})]});}
            var Q3;
            {var subQ0=sQuery(id+"F0.wireOp",EDGE,"E4.left");var subQ1=sQuery(id+"F0.wireOp",EDGE,"E4.top");var subQ2=sQuery(id+"F0.wireOp",EDGE,"E9");var subQ3=sQuery(id+"F0.wireOp",EDGE,"E7.top");var subQ4=sQuery(id+"F0.wireOp",EDGE,"E6.left");Q3=makeQuery(id+"F12.opFillet","BLEND_EDGE",EDGE,{"blendedFrom":[makeQuery(id+"F11.opFillet","BLEND_EDGE",EDGE,{"disambiguationData":[OD(0.0)],"blendedFrom":[makeQuery(id+"F9.opFillet","BLEND_EDGE",EDGE,{"blendedFrom":[makeQuery(id+"F2.opExtrude","SWEPT_EDGE",EDGE,{"disambiguationData":[OSD([subQ4,subQ3])]}),makeQuery(id+"F4.opExtrude","CAP_FACE",FACE,{"disambiguationData":[OSD([subQ1,subQ0,subQ4,subQ3,subQ2,sQuery(id+"F0.wireOp",EDGE,"E12")])],"isStart":false})],"blendedInto":[makeQuery(id+"F4.opExtrude","CAP_FACE",FACE,{"disambiguationData":[OSD([subQ1,subQ0,subQ4,subQ3,subQ2,sQuery(id+"F0.wireOp",EDGE,"E12")])],"isStart":false})]}),makeQuery(id+"F4.opExtrude","SWEPT_FACE",FACE,{"disambiguationData":[OSD([subQ2])]})],"blendedInto":[makeQuery(id+"F4.opExtrude","SWEPT_FACE",FACE,{"disambiguationData":[OSD([subQ2])]})]}),makeQuery(id+"F4.opExtrude","SWEPT_FACE",FACE,{"disambiguationData":[OSD([subQ1]),TDD([makeQuery(id+"F0.imprint","IMPRINT",EDGE,{"disambiguationData":[TD([[makeQuery(id+"F0.imprint","INTERSECT",VERTEX,{"derivedFrom":[subQ1,subQ0]}),-1.0]])],"derivedFrom":subQ1})])]})],"blendedInto":[makeQuery(id+"F4.opExtrude","SWEPT_FACE",FACE,{"disambiguationData":[OSD([subQ1]),TDD([makeQuery(id+"F0.imprint","IMPRINT",EDGE,{"disambiguationData":[TD([[makeQuery(id+"F0.imprint","INTERSECT",VERTEX,{"derivedFrom":[subQ1,subQ0]}),-1.0]])],"derivedFrom":subQ1})])]})]});}
            var Q4;
            {var subQ0=sQuery(id+"F0.wireOp",EDGE,"E4.right");var subQ1=sQuery(id+"F0.wireOp",EDGE,"E4.top");var subQ2=sQuery(id+"F0.wireOp",EDGE,"E8");var subQ3=sQuery(id+"F0.wireOp",EDGE,"E7.top");var subQ4=sQuery(id+"F0.wireOp",EDGE,"E6.right");Q4=makeQuery(id+"F12.opFillet","BLEND_EDGE",EDGE,{"blendedFrom":[makeQuery(id+"F11.opFillet","BLEND_EDGE",EDGE,{"blendedFrom":[makeQuery(id+"F9.opFillet","BLEND_EDGE",EDGE,{"blendedFrom":[makeQuery(id+"F2.opExtrude","SWEPT_EDGE",EDGE,{"disambiguationData":[OSD([subQ4,subQ3])]}),makeQuery(id+"F4.opExtrude","CAP_FACE",FACE,{"disambiguationData":[OSD([subQ1,subQ0,subQ4,subQ3,subQ2,sQuery(id+"F0.wireOp",EDGE,"E11")])],"isStart":false})],"blendedInto":[makeQuery(id+"F4.opExtrude","CAP_FACE",FACE,{"disambiguationData":[OSD([subQ1,subQ0,subQ4,subQ3,subQ2,sQuery(id+"F0.wireOp",EDGE,"E11")])],"isStart":false})]}),makeQuery(id+"F4.opExtrude","SWEPT_FACE",FACE,{"disambiguationData":[OSD([subQ2])]})],"blendedInto":[makeQuery(id+"F4.opExtrude","SWEPT_FACE",FACE,{"disambiguationData":[OSD([subQ2])]})]}),makeQuery(id+"F4.opExtrude","SWEPT_FACE",FACE,{"disambiguationData":[OSD([subQ1]),TDD([makeQuery(id+"F0.imprint","IMPRINT",EDGE,{"disambiguationData":[TD([[makeQuery(id+"F0.imprint","INTERSECT",VERTEX,{"derivedFrom":[subQ1,subQ0]}),1.0]])],"derivedFrom":subQ1})])]})],"blendedInto":[makeQuery(id+"F4.opExtrude","SWEPT_FACE",FACE,{"disambiguationData":[OSD([subQ1]),TDD([makeQuery(id+"F0.imprint","IMPRINT",EDGE,{"disambiguationData":[TD([[makeQuery(id+"F0.imprint","INTERSECT",VERTEX,{"derivedFrom":[subQ1,subQ0]}),1.0]])],"derivedFrom":subQ1})])]})]});}
            var Q5;
            {var subQ0=sQuery(id+"F0.wireOp",EDGE,"E11");var subQ1=sQuery(id+"F0.wireOp",EDGE,"E7.top");var subQ2=sQuery(id+"F0.wireOp",EDGE,"E6.right");Q5=makeQuery(id+"F11.opFillet","BLEND_EDGE",EDGE,{"blendedFrom":[makeQuery(id+"F9.opFillet","BLEND_EDGE",EDGE,{"blendedFrom":[makeQuery(id+"F2.opExtrude","SWEPT_EDGE",EDGE,{"disambiguationData":[OSD([subQ2,subQ1])]}),makeQuery(id+"F4.opExtrude","CAP_FACE",FACE,{"disambiguationData":[OSD([sQuery(id+"F0.wireOp",EDGE,"E4.top"),sQuery(id+"F0.wireOp",EDGE,"E4.right"),subQ2,subQ1,sQuery(id+"F0.wireOp",EDGE,"E8"),subQ0])],"isStart":false})],"blendedInto":[makeQuery(id+"F4.opExtrude","CAP_FACE",FACE,{"disambiguationData":[OSD([sQuery(id+"F0.wireOp",EDGE,"E4.top"),sQuery(id+"F0.wireOp",EDGE,"E4.right"),subQ2,subQ1,sQuery(id+"F0.wireOp",EDGE,"E8"),subQ0])],"isStart":false})]}),makeQuery(id+"F10.opFillet","BLEND_FACE",FACE,{"disambiguationData":[OSD([sQuery(id+"F0.wireOp",EDGE,"E5.right"),sQuery(id+"F0.wireOp",EDGE,"E7.bottom"),subQ1,sQuery(id+"F0.wireOp",EDGE,"E10"),subQ0])]})],"blendedInto":[makeQuery(id+"F10.opFillet","BLEND_FACE",FACE,{"disambiguationData":[OSD([sQuery(id+"F0.wireOp",EDGE,"E5.right"),sQuery(id+"F0.wireOp",EDGE,"E7.bottom"),subQ1,sQuery(id+"F0.wireOp",EDGE,"E10"),subQ0])]})]});}
            var Q6;
            {var subQ0=sQuery(id+"F0.wireOp",EDGE,"E4.right");var subQ1=sQuery(id+"F0.wireOp",EDGE,"E4.bottom");var subQ2=makeQuery(id+"F0.imprint","INTERSECT",VERTEX,{"derivedFrom":[subQ1,subQ0]});var subQ3=sQuery(id+"F0.wireOp",EDGE,"E14");var subQ4=sQuery(id+"F0.wireOp",EDGE,"E7.bottom");var subQ5=sQuery(id+"F0.wireOp",EDGE,"E6.right");Q6=makeQuery(id+"F12.opFillet","BLEND_EDGE",EDGE,{"blendedFrom":[makeQuery(id+"F11.opFillet","BLEND_EDGE",EDGE,{"blendedFrom":[makeQuery(id+"F9.opFillet","BLEND_EDGE",EDGE,{"blendedFrom":[makeQuery(id+"F2.opExtrude","SWEPT_EDGE",EDGE,{"disambiguationData":[OSD([subQ5,subQ4])]}),makeQuery(id+"F4.opExtrude","CAP_FACE",FACE,{"disambiguationData":[OSD([subQ1,subQ0,subQ5,subQ4,sQuery(id+"F0.wireOp",EDGE,"E10"),subQ3])],"isStart":false})],"blendedInto":[makeQuery(id+"F4.opExtrude","CAP_FACE",FACE,{"disambiguationData":[OSD([subQ1,subQ0,subQ5,subQ4,sQuery(id+"F0.wireOp",EDGE,"E10"),subQ3])],"isStart":false})]}),makeQuery(id+"F4.opExtrude","SWEPT_FACE",FACE,{"disambiguationData":[OSD([subQ0]),TDD([makeQuery(id+"F0.imprint","IMPRINT",EDGE,{"disambiguationData":[TD([[subQ2,-1.0]])],"derivedFrom":subQ0})])]})],"blendedInto":[makeQuery(id+"F4.opExtrude","SWEPT_FACE",FACE,{"disambiguationData":[OSD([subQ0]),TDD([makeQuery(id+"F0.imprint","IMPRINT",EDGE,{"disambiguationData":[TD([[subQ2,-1.0]])],"derivedFrom":subQ0})])]})]}),makeQuery(id+"F4.opExtrude","SWEPT_FACE",FACE,{"disambiguationData":[OSD([subQ1]),TDD([makeQuery(id+"F0.imprint","IMPRINT",EDGE,{"disambiguationData":[TD([[subQ2,1.0]])],"derivedFrom":subQ1})])]})],"blendedInto":[makeQuery(id+"F4.opExtrude","SWEPT_FACE",FACE,{"disambiguationData":[OSD([subQ1]),TDD([makeQuery(id+"F0.imprint","IMPRINT",EDGE,{"disambiguationData":[TD([[subQ2,1.0]])],"derivedFrom":subQ1})])]})]});}
            var Q7;
            {var subQ0=sQuery(id+"F0.wireOp",EDGE,"E4.right");var subQ1=sQuery(id+"F0.wireOp",EDGE,"E4.bottom");var subQ2=sQuery(id+"F0.wireOp",EDGE,"E14");var subQ3=sQuery(id+"F0.wireOp",EDGE,"E7.bottom");var subQ4=sQuery(id+"F0.wireOp",EDGE,"E6.right");Q7=makeQuery(id+"F12.opFillet","BLEND_EDGE",EDGE,{"blendedFrom":[makeQuery(id+"F11.opFillet","BLEND_EDGE",EDGE,{"disambiguationData":[OD(0.0)],"blendedFrom":[makeQuery(id+"F9.opFillet","BLEND_EDGE",EDGE,{"blendedFrom":[makeQuery(id+"F2.opExtrude","SWEPT_EDGE",EDGE,{"disambiguationData":[OSD([subQ4,subQ3])]}),makeQuery(id+"F4.opExtrude","CAP_FACE",FACE,{"disambiguationData":[OSD([subQ1,subQ0,subQ4,subQ3,sQuery(id+"F0.wireOp",EDGE,"E10"),subQ2])],"isStart":false})],"blendedInto":[makeQuery(id+"F4.opExtrude","CAP_FACE",FACE,{"disambiguationData":[OSD([subQ1,subQ0,subQ4,subQ3,sQuery(id+"F0.wireOp",EDGE,"E10"),subQ2])],"isStart":false})]}),makeQuery(id+"F4.opExtrude","SWEPT_FACE",FACE,{"disambiguationData":[OSD([subQ2])]})],"blendedInto":[makeQuery(id+"F4.opExtrude","SWEPT_FACE",FACE,{"disambiguationData":[OSD([subQ2])]})]}),makeQuery(id+"F4.opExtrude","SWEPT_FACE",FACE,{"disambiguationData":[OSD([subQ1]),TDD([makeQuery(id+"F0.imprint","IMPRINT",EDGE,{"disambiguationData":[TD([[makeQuery(id+"F0.imprint","INTERSECT",VERTEX,{"derivedFrom":[subQ1,subQ0]}),1.0]])],"derivedFrom":subQ1})])]})],"blendedInto":[makeQuery(id+"F4.opExtrude","SWEPT_FACE",FACE,{"disambiguationData":[OSD([subQ1]),TDD([makeQuery(id+"F0.imprint","IMPRINT",EDGE,{"disambiguationData":[TD([[makeQuery(id+"F0.imprint","INTERSECT",VERTEX,{"derivedFrom":[subQ1,subQ0]}),1.0]])],"derivedFrom":subQ1})])]})]});}
            var Q8;
            {var subQ0=sQuery(id+"F0.wireOp",EDGE,"E4.left");var subQ1=sQuery(id+"F0.wireOp",EDGE,"E4.bottom");var subQ2=sQuery(id+"F0.wireOp",EDGE,"E15");var subQ3=sQuery(id+"F0.wireOp",EDGE,"E7.bottom");var subQ4=sQuery(id+"F0.wireOp",EDGE,"E6.left");Q8=makeQuery(id+"F12.opFillet","BLEND_EDGE",EDGE,{"blendedFrom":[makeQuery(id+"F11.opFillet","BLEND_EDGE",EDGE,{"blendedFrom":[makeQuery(id+"F9.opFillet","BLEND_EDGE",EDGE,{"blendedFrom":[makeQuery(id+"F2.opExtrude","SWEPT_EDGE",EDGE,{"disambiguationData":[OSD([subQ4,subQ3])]}),makeQuery(id+"F4.opExtrude","CAP_FACE",FACE,{"disambiguationData":[OSD([subQ1,subQ0,subQ4,subQ3,sQuery(id+"F0.wireOp",EDGE,"E13"),subQ2])],"isStart":false})],"blendedInto":[makeQuery(id+"F4.opExtrude","CAP_FACE",FACE,{"disambiguationData":[OSD([subQ1,subQ0,subQ4,subQ3,sQuery(id+"F0.wireOp",EDGE,"E13"),subQ2])],"isStart":false})]}),makeQuery(id+"F4.opExtrude","SWEPT_FACE",FACE,{"disambiguationData":[OSD([subQ2])]})],"blendedInto":[makeQuery(id+"F4.opExtrude","SWEPT_FACE",FACE,{"disambiguationData":[OSD([subQ2])]})]}),makeQuery(id+"F4.opExtrude","SWEPT_FACE",FACE,{"disambiguationData":[OSD([subQ1]),TDD([makeQuery(id+"F0.imprint","IMPRINT",EDGE,{"disambiguationData":[TD([[makeQuery(id+"F0.imprint","INTERSECT",VERTEX,{"derivedFrom":[subQ1,subQ0]}),-1.0]])],"derivedFrom":subQ1})])]})],"blendedInto":[makeQuery(id+"F4.opExtrude","SWEPT_FACE",FACE,{"disambiguationData":[OSD([subQ1]),TDD([makeQuery(id+"F0.imprint","IMPRINT",EDGE,{"disambiguationData":[TD([[makeQuery(id+"F0.imprint","INTERSECT",VERTEX,{"derivedFrom":[subQ1,subQ0]}),-1.0]])],"derivedFrom":subQ1})])]})]});}
            var Q9;
            {var subQ0=sQuery(id+"F0.wireOp",EDGE,"E4.left");var subQ1=sQuery(id+"F0.wireOp",EDGE,"E4.bottom");var subQ2=makeQuery(id+"F0.imprint","INTERSECT",VERTEX,{"derivedFrom":[subQ1,subQ0]});var subQ3=sQuery(id+"F0.wireOp",EDGE,"E15");var subQ4=sQuery(id+"F0.wireOp",EDGE,"E7.bottom");var subQ5=sQuery(id+"F0.wireOp",EDGE,"E6.left");Q9=makeQuery(id+"F12.opFillet","BLEND_EDGE",EDGE,{"blendedFrom":[makeQuery(id+"F11.opFillet","BLEND_EDGE",EDGE,{"blendedFrom":[makeQuery(id+"F9.opFillet","BLEND_EDGE",EDGE,{"blendedFrom":[makeQuery(id+"F2.opExtrude","SWEPT_EDGE",EDGE,{"disambiguationData":[OSD([subQ5,subQ4])]}),makeQuery(id+"F4.opExtrude","CAP_FACE",FACE,{"disambiguationData":[OSD([subQ1,subQ0,subQ5,subQ4,sQuery(id+"F0.wireOp",EDGE,"E13"),subQ3])],"isStart":false})],"blendedInto":[makeQuery(id+"F4.opExtrude","CAP_FACE",FACE,{"disambiguationData":[OSD([subQ1,subQ0,subQ5,subQ4,sQuery(id+"F0.wireOp",EDGE,"E13"),subQ3])],"isStart":false})]}),makeQuery(id+"F4.opExtrude","SWEPT_FACE",FACE,{"disambiguationData":[OSD([subQ0]),TDD([makeQuery(id+"F0.imprint","IMPRINT",EDGE,{"disambiguationData":[TD([[subQ2,-1.0]])],"derivedFrom":subQ0})])]})],"blendedInto":[makeQuery(id+"F4.opExtrude","SWEPT_FACE",FACE,{"disambiguationData":[OSD([subQ0]),TDD([makeQuery(id+"F0.imprint","IMPRINT",EDGE,{"disambiguationData":[TD([[subQ2,-1.0]])],"derivedFrom":subQ0})])]})]}),makeQuery(id+"F4.opExtrude","SWEPT_FACE",FACE,{"disambiguationData":[OSD([subQ1]),TDD([makeQuery(id+"F0.imprint","IMPRINT",EDGE,{"disambiguationData":[TD([[subQ2,-1.0]])],"derivedFrom":subQ1})])]})],"blendedInto":[makeQuery(id+"F4.opExtrude","SWEPT_FACE",FACE,{"disambiguationData":[OSD([subQ1]),TDD([makeQuery(id+"F0.imprint","IMPRINT",EDGE,{"disambiguationData":[TD([[subQ2,-1.0]])],"derivedFrom":subQ1})])]})]});}
            var Q10;
            {var subQ0=sQuery(id+"F0.wireOp",EDGE,"E7.top");var subQ1=sQuery(id+"F0.wireOp",EDGE,"E6.right");var subQ2=sQuery(id+"F0.wireOp",EDGE,"E4.right");var subQ3=sQuery(id+"F0.wireOp",EDGE,"E4.top");var subQ4=sQuery(id+"F0.wireOp",EDGE,"E6.left");var subQ5=sQuery(id+"F0.wireOp",EDGE,"E4.left");var subQ6=sQuery(id+"F0.wireOp",EDGE,"E14");var subQ7=sQuery(id+"F0.wireOp",EDGE,"E7.bottom");var subQ8=sQuery(id+"F0.wireOp",EDGE,"E4.bottom");var subQ9=sQuery(id+"F0.wireOp",EDGE,"E15");Q10=makeQuery(id+"F10.opFillet","BLEND_EDGE",EDGE,{"blendedFrom":[makeQuery(id+"F4.boolean.opBoolean","MERGE",EDGE,{"derivedFrom":[makeQuery(id+"F4.opExtrude","SWEPT_EDGE",EDGE,{"disambiguationData":[OSD([subQ7,subQ6,subQ9]),OD(0.0)]}),makeQuery(id+"F4.opExtrude","SWEPT_EDGE",EDGE,{"disambiguationData":[OSD([subQ7,subQ6,subQ9]),OD(1.0)]})]}),makeQuery(id+"F4.boolean.opBoolean","MERGE",FACE,{"derivedFrom":[makeQuery(id+"F2.opExtrude","CAP_FACE",FACE,{"disambiguationData":[OSD([sQuery(id+"F0.wireOp",EDGE,"E0"),sQuery(id+"F0.wireOp",EDGE,"E2"),sQuery(id+"F0.wireOp",EDGE,"E3.1.1"),sQuery(id+"F0.wireOp",EDGE,"E3.2.1"),sQuery(id+"F0.wireOp",EDGE,"E3.3.1"),subQ4,subQ1,subQ7,subQ0])],"isStart":true}),makeQuery(id+"F4.opExtrude","CAP_FACE",FACE,{"disambiguationData":[OSD([subQ8,subQ5,subQ4,subQ7,sQuery(id+"F0.wireOp",EDGE,"E13"),subQ9])],"isStart":true}),makeQuery(id+"F4.opExtrude","CAP_FACE",FACE,{"disambiguationData":[OSD([subQ8,subQ2,subQ1,subQ7,sQuery(id+"F0.wireOp",EDGE,"E10"),subQ6])],"isStart":true}),makeQuery(id+"F4.opExtrude","CAP_FACE",FACE,{"disambiguationData":[OSD([subQ3,subQ5,subQ4,subQ0,sQuery(id+"F0.wireOp",EDGE,"E9"),sQuery(id+"F0.wireOp",EDGE,"E12")])],"isStart":true}),makeQuery(id+"F4.opExtrude","CAP_FACE",FACE,{"disambiguationData":[OSD([subQ3,subQ2,subQ1,subQ0,sQuery(id+"F0.wireOp",EDGE,"E8"),sQuery(id+"F0.wireOp",EDGE,"E11")])],"isStart":true})]})],"blendedInto":[makeQuery(id+"F4.boolean.opBoolean","MERGE",FACE,{"derivedFrom":[makeQuery(id+"F2.opExtrude","CAP_FACE",FACE,{"disambiguationData":[OSD([sQuery(id+"F0.wireOp",EDGE,"E0"),sQuery(id+"F0.wireOp",EDGE,"E2"),sQuery(id+"F0.wireOp",EDGE,"E3.1.1"),sQuery(id+"F0.wireOp",EDGE,"E3.2.1"),sQuery(id+"F0.wireOp",EDGE,"E3.3.1"),subQ4,subQ1,subQ7,subQ0])],"isStart":true}),makeQuery(id+"F4.opExtrude","CAP_FACE",FACE,{"disambiguationData":[OSD([subQ8,subQ5,subQ4,subQ7,sQuery(id+"F0.wireOp",EDGE,"E13"),subQ9])],"isStart":true}),makeQuery(id+"F4.opExtrude","CAP_FACE",FACE,{"disambiguationData":[OSD([subQ8,subQ2,subQ1,subQ7,sQuery(id+"F0.wireOp",EDGE,"E10"),subQ6])],"isStart":true}),makeQuery(id+"F4.opExtrude","CAP_FACE",FACE,{"disambiguationData":[OSD([subQ3,subQ5,subQ4,subQ0,sQuery(id+"F0.wireOp",EDGE,"E9"),sQuery(id+"F0.wireOp",EDGE,"E12")])],"isStart":true}),makeQuery(id+"F4.opExtrude","CAP_FACE",FACE,{"disambiguationData":[OSD([subQ3,subQ2,subQ1,subQ0,sQuery(id+"F0.wireOp",EDGE,"E8"),sQuery(id+"F0.wireOp",EDGE,"E11")])],"isStart":true})]})]});}
            var Q11;
            {var subQ0=sQuery(id+"F0.wireOp",EDGE,"E8");var subQ1=sQuery(id+"F0.wireOp",EDGE,"E7.top");var subQ2=sQuery(id+"F0.wireOp",EDGE,"E6.right");var subQ3=sQuery(id+"F0.wireOp",EDGE,"E4.right");var subQ4=sQuery(id+"F0.wireOp",EDGE,"E4.top");var subQ5=sQuery(id+"F0.wireOp",EDGE,"E9");var subQ6=sQuery(id+"F0.wireOp",EDGE,"E6.left");var subQ7=sQuery(id+"F0.wireOp",EDGE,"E4.left");var subQ8=sQuery(id+"F0.wireOp",EDGE,"E7.bottom");var subQ9=sQuery(id+"F0.wireOp",EDGE,"E4.bottom");Q11=makeQuery(id+"F10.opFillet","BLEND_EDGE",EDGE,{"blendedFrom":[makeQuery(id+"F4.boolean.opBoolean","MERGE",EDGE,{"derivedFrom":[makeQuery(id+"F4.opExtrude","SWEPT_EDGE",EDGE,{"disambiguationData":[OSD([subQ1,subQ0,subQ5]),OD(0.0)]}),makeQuery(id+"F4.opExtrude","SWEPT_EDGE",EDGE,{"disambiguationData":[OSD([subQ1,subQ0,subQ5]),OD(1.0)]})]}),makeQuery(id+"F4.boolean.opBoolean","MERGE",FACE,{"derivedFrom":[makeQuery(id+"F2.opExtrude","CAP_FACE",FACE,{"disambiguationData":[OSD([sQuery(id+"F0.wireOp",EDGE,"E0"),sQuery(id+"F0.wireOp",EDGE,"E2"),sQuery(id+"F0.wireOp",EDGE,"E3.1.1"),sQuery(id+"F0.wireOp",EDGE,"E3.2.1"),sQuery(id+"F0.wireOp",EDGE,"E3.3.1"),subQ6,subQ2,subQ8,subQ1])],"isStart":true}),makeQuery(id+"F4.opExtrude","CAP_FACE",FACE,{"disambiguationData":[OSD([subQ9,subQ7,subQ6,subQ8,sQuery(id+"F0.wireOp",EDGE,"E13"),sQuery(id+"F0.wireOp",EDGE,"E15")])],"isStart":true}),makeQuery(id+"F4.opExtrude","CAP_FACE",FACE,{"disambiguationData":[OSD([subQ9,subQ3,subQ2,subQ8,sQuery(id+"F0.wireOp",EDGE,"E10"),sQuery(id+"F0.wireOp",EDGE,"E14")])],"isStart":true}),makeQuery(id+"F4.opExtrude","CAP_FACE",FACE,{"disambiguationData":[OSD([subQ4,subQ7,subQ6,subQ1,subQ5,sQuery(id+"F0.wireOp",EDGE,"E12")])],"isStart":true}),makeQuery(id+"F4.opExtrude","CAP_FACE",FACE,{"disambiguationData":[OSD([subQ4,subQ3,subQ2,subQ1,subQ0,sQuery(id+"F0.wireOp",EDGE,"E11")])],"isStart":true})]})],"blendedInto":[makeQuery(id+"F4.boolean.opBoolean","MERGE",FACE,{"derivedFrom":[makeQuery(id+"F2.opExtrude","CAP_FACE",FACE,{"disambiguationData":[OSD([sQuery(id+"F0.wireOp",EDGE,"E0"),sQuery(id+"F0.wireOp",EDGE,"E2"),sQuery(id+"F0.wireOp",EDGE,"E3.1.1"),sQuery(id+"F0.wireOp",EDGE,"E3.2.1"),sQuery(id+"F0.wireOp",EDGE,"E3.3.1"),subQ6,subQ2,subQ8,subQ1])],"isStart":true}),makeQuery(id+"F4.opExtrude","CAP_FACE",FACE,{"disambiguationData":[OSD([subQ9,subQ7,subQ6,subQ8,sQuery(id+"F0.wireOp",EDGE,"E13"),sQuery(id+"F0.wireOp",EDGE,"E15")])],"isStart":true}),makeQuery(id+"F4.opExtrude","CAP_FACE",FACE,{"disambiguationData":[OSD([subQ9,subQ3,subQ2,subQ8,sQuery(id+"F0.wireOp",EDGE,"E10"),sQuery(id+"F0.wireOp",EDGE,"E14")])],"isStart":true}),makeQuery(id+"F4.opExtrude","CAP_FACE",FACE,{"disambiguationData":[OSD([subQ4,subQ7,subQ6,subQ1,subQ5,sQuery(id+"F0.wireOp",EDGE,"E12")])],"isStart":true}),makeQuery(id+"F4.opExtrude","CAP_FACE",FACE,{"disambiguationData":[OSD([subQ4,subQ3,subQ2,subQ1,subQ0,sQuery(id+"F0.wireOp",EDGE,"E11")])],"isStart":true})]})]});}
            var Q12;
            {var subQ0=sQuery(id+"F0.wireOp",EDGE,"E7.top");var subQ1=sQuery(id+"F0.wireOp",EDGE,"E6.right");var subQ2=sQuery(id+"F0.wireOp",EDGE,"E4.right");var subQ3=sQuery(id+"F0.wireOp",EDGE,"E4.top");var subQ4=sQuery(id+"F0.wireOp",EDGE,"E12");var subQ5=sQuery(id+"F0.wireOp",EDGE,"E6.left");var subQ6=sQuery(id+"F0.wireOp",EDGE,"E4.left");var subQ7=sQuery(id+"F0.wireOp",EDGE,"E7.bottom");var subQ8=sQuery(id+"F0.wireOp",EDGE,"E4.bottom");var subQ9=sQuery(id+"F0.wireOp",EDGE,"E13");var subQ10=sQuery(id+"F0.wireOp",EDGE,"E5.left");Q12=makeQuery(id+"F10.opFillet","BLEND_EDGE",EDGE,{"blendedFrom":[makeQuery(id+"F8.opFillet","BLEND_EDGE",EDGE,{"blendedFrom":[makeQuery(id+"F4.opExtrude","SWEPT_EDGE",EDGE,{"disambiguationData":[OSD([subQ10,subQ0,subQ4])]}),makeQuery(id+"F4.opExtrude","SWEPT_EDGE",EDGE,{"disambiguationData":[OSD([subQ10,subQ7,subQ9])]})],"blendedInto":[]}),makeQuery(id+"F4.boolean.opBoolean","MERGE",FACE,{"derivedFrom":[makeQuery(id+"F2.opExtrude","CAP_FACE",FACE,{"disambiguationData":[OSD([sQuery(id+"F0.wireOp",EDGE,"E0"),sQuery(id+"F0.wireOp",EDGE,"E2"),sQuery(id+"F0.wireOp",EDGE,"E3.1.1"),sQuery(id+"F0.wireOp",EDGE,"E3.2.1"),sQuery(id+"F0.wireOp",EDGE,"E3.3.1"),subQ5,subQ1,subQ7,subQ0])],"isStart":true}),makeQuery(id+"F4.opExtrude","CAP_FACE",FACE,{"disambiguationData":[OSD([subQ8,subQ6,subQ5,subQ7,subQ9,sQuery(id+"F0.wireOp",EDGE,"E15")])],"isStart":true}),makeQuery(id+"F4.opExtrude","CAP_FACE",FACE,{"disambiguationData":[OSD([subQ8,subQ2,subQ1,subQ7,sQuery(id+"F0.wireOp",EDGE,"E10"),sQuery(id+"F0.wireOp",EDGE,"E14")])],"isStart":true}),makeQuery(id+"F4.opExtrude","CAP_FACE",FACE,{"disambiguationData":[OSD([subQ3,subQ6,subQ5,subQ0,sQuery(id+"F0.wireOp",EDGE,"E9"),subQ4])],"isStart":true}),makeQuery(id+"F4.opExtrude","CAP_FACE",FACE,{"disambiguationData":[OSD([subQ3,subQ2,subQ1,subQ0,sQuery(id+"F0.wireOp",EDGE,"E8"),sQuery(id+"F0.wireOp",EDGE,"E11")])],"isStart":true})]})],"blendedInto":[makeQuery(id+"F4.boolean.opBoolean","MERGE",FACE,{"derivedFrom":[makeQuery(id+"F2.opExtrude","CAP_FACE",FACE,{"disambiguationData":[OSD([sQuery(id+"F0.wireOp",EDGE,"E0"),sQuery(id+"F0.wireOp",EDGE,"E2"),sQuery(id+"F0.wireOp",EDGE,"E3.1.1"),sQuery(id+"F0.wireOp",EDGE,"E3.2.1"),sQuery(id+"F0.wireOp",EDGE,"E3.3.1"),subQ5,subQ1,subQ7,subQ0])],"isStart":true}),makeQuery(id+"F4.opExtrude","CAP_FACE",FACE,{"disambiguationData":[OSD([subQ8,subQ6,subQ5,subQ7,subQ9,sQuery(id+"F0.wireOp",EDGE,"E15")])],"isStart":true}),makeQuery(id+"F4.opExtrude","CAP_FACE",FACE,{"disambiguationData":[OSD([subQ8,subQ2,subQ1,subQ7,sQuery(id+"F0.wireOp",EDGE,"E10"),sQuery(id+"F0.wireOp",EDGE,"E14")])],"isStart":true}),makeQuery(id+"F4.opExtrude","CAP_FACE",FACE,{"disambiguationData":[OSD([subQ3,subQ6,subQ5,subQ0,sQuery(id+"F0.wireOp",EDGE,"E9"),subQ4])],"isStart":true}),makeQuery(id+"F4.opExtrude","CAP_FACE",FACE,{"disambiguationData":[OSD([subQ3,subQ2,subQ1,subQ0,sQuery(id+"F0.wireOp",EDGE,"E8"),sQuery(id+"F0.wireOp",EDGE,"E11")])],"isStart":true})]})]});}
            var Q13;
            {var subQ0=sQuery(id+"F0.wireOp",EDGE,"E11");var subQ1=sQuery(id+"F0.wireOp",EDGE,"E7.top");var subQ2=sQuery(id+"F0.wireOp",EDGE,"E6.right");var subQ3=sQuery(id+"F0.wireOp",EDGE,"E4.right");var subQ4=sQuery(id+"F0.wireOp",EDGE,"E4.top");var subQ5=sQuery(id+"F0.wireOp",EDGE,"E6.left");var subQ6=sQuery(id+"F0.wireOp",EDGE,"E4.left");var subQ7=sQuery(id+"F0.wireOp",EDGE,"E10");var subQ8=sQuery(id+"F0.wireOp",EDGE,"E7.bottom");var subQ9=sQuery(id+"F0.wireOp",EDGE,"E4.bottom");var subQ10=sQuery(id+"F0.wireOp",EDGE,"E5.right");Q13=makeQuery(id+"F10.opFillet","BLEND_EDGE",EDGE,{"blendedFrom":[makeQuery(id+"F8.opFillet","BLEND_EDGE",EDGE,{"blendedFrom":[makeQuery(id+"F4.opExtrude","SWEPT_EDGE",EDGE,{"disambiguationData":[OSD([subQ10,subQ8,subQ7])]}),makeQuery(id+"F4.opExtrude","SWEPT_EDGE",EDGE,{"disambiguationData":[OSD([subQ10,subQ1,subQ0])]})],"blendedInto":[]}),makeQuery(id+"F4.boolean.opBoolean","MERGE",FACE,{"derivedFrom":[makeQuery(id+"F2.opExtrude","CAP_FACE",FACE,{"disambiguationData":[OSD([sQuery(id+"F0.wireOp",EDGE,"E0"),sQuery(id+"F0.wireOp",EDGE,"E2"),sQuery(id+"F0.wireOp",EDGE,"E3.1.1"),sQuery(id+"F0.wireOp",EDGE,"E3.2.1"),sQuery(id+"F0.wireOp",EDGE,"E3.3.1"),subQ5,subQ2,subQ8,subQ1])],"isStart":true}),makeQuery(id+"F4.opExtrude","CAP_FACE",FACE,{"disambiguationData":[OSD([subQ9,subQ6,subQ5,subQ8,sQuery(id+"F0.wireOp",EDGE,"E13"),sQuery(id+"F0.wireOp",EDGE,"E15")])],"isStart":true}),makeQuery(id+"F4.opExtrude","CAP_FACE",FACE,{"disambiguationData":[OSD([subQ9,subQ3,subQ2,subQ8,subQ7,sQuery(id+"F0.wireOp",EDGE,"E14")])],"isStart":true}),makeQuery(id+"F4.opExtrude","CAP_FACE",FACE,{"disambiguationData":[OSD([subQ4,subQ6,subQ5,subQ1,sQuery(id+"F0.wireOp",EDGE,"E9"),sQuery(id+"F0.wireOp",EDGE,"E12")])],"isStart":true}),makeQuery(id+"F4.opExtrude","CAP_FACE",FACE,{"disambiguationData":[OSD([subQ4,subQ3,subQ2,subQ1,sQuery(id+"F0.wireOp",EDGE,"E8"),subQ0])],"isStart":true})]})],"blendedInto":[makeQuery(id+"F4.boolean.opBoolean","MERGE",FACE,{"derivedFrom":[makeQuery(id+"F2.opExtrude","CAP_FACE",FACE,{"disambiguationData":[OSD([sQuery(id+"F0.wireOp",EDGE,"E0"),sQuery(id+"F0.wireOp",EDGE,"E2"),sQuery(id+"F0.wireOp",EDGE,"E3.1.1"),sQuery(id+"F0.wireOp",EDGE,"E3.2.1"),sQuery(id+"F0.wireOp",EDGE,"E3.3.1"),subQ5,subQ2,subQ8,subQ1])],"isStart":true}),makeQuery(id+"F4.opExtrude","CAP_FACE",FACE,{"disambiguationData":[OSD([subQ9,subQ6,subQ5,subQ8,sQuery(id+"F0.wireOp",EDGE,"E13"),sQuery(id+"F0.wireOp",EDGE,"E15")])],"isStart":true}),makeQuery(id+"F4.opExtrude","CAP_FACE",FACE,{"disambiguationData":[OSD([subQ9,subQ3,subQ2,subQ8,subQ7,sQuery(id+"F0.wireOp",EDGE,"E14")])],"isStart":true}),makeQuery(id+"F4.opExtrude","CAP_FACE",FACE,{"disambiguationData":[OSD([subQ4,subQ6,subQ5,subQ1,sQuery(id+"F0.wireOp",EDGE,"E9"),sQuery(id+"F0.wireOp",EDGE,"E12")])],"isStart":true}),makeQuery(id+"F4.opExtrude","CAP_FACE",FACE,{"disambiguationData":[OSD([subQ4,subQ3,subQ2,subQ1,sQuery(id+"F0.wireOp",EDGE,"E8"),subQ0])],"isStart":true})]})]});}
            var Q14;
            {var subQ0=sQuery(id+"F0.wireOp",EDGE,"E4.bottom");Q14=makeQuery(id+"F4.opExtrude","CAP_EDGE",EDGE,{"disambiguationData":[OSD([subQ0]),TDD([makeQuery(id+"F0.imprint","IMPRINT",EDGE,{"disambiguationData":[TD([[makeQuery(id+"F0.imprint","INTERSECT",VERTEX,{"derivedFrom":[subQ0,sQuery(id+"F0.wireOp",EDGE,"E4.left")]}),-1.0]])],"derivedFrom":subQ0})])],"isStart":true});}
            var Q15;
            {var subQ0=sQuery(id+"F0.wireOp",EDGE,"E4.left");Q15=makeQuery(id+"F4.opExtrude","CAP_EDGE",EDGE,{"disambiguationData":[OSD([subQ0]),TDD([makeQuery(id+"F0.imprint","IMPRINT",EDGE,{"disambiguationData":[TD([[makeQuery(id+"F0.imprint","INTERSECT",VERTEX,{"derivedFrom":[sQuery(id+"F0.wireOp",EDGE,"E4.bottom"),subQ0]}),-1.0]])],"derivedFrom":subQ0})])],"isStart":true});}
            var Q16;
            {var subQ0=sQuery(id+"F0.wireOp",EDGE,"E4.left");Q16=makeQuery(id+"F4.opExtrude","CAP_EDGE",EDGE,{"disambiguationData":[OSD([subQ0]),TDD([makeQuery(id+"F0.imprint","IMPRINT",EDGE,{"disambiguationData":[TD([[makeQuery(id+"F0.imprint","INTERSECT",VERTEX,{"derivedFrom":[sQuery(id+"F0.wireOp",EDGE,"E4.top"),subQ0]}),1.0]])],"derivedFrom":subQ0})])],"isStart":true});}
            var Q17;
            {var subQ0=sQuery(id+"F0.wireOp",EDGE,"E4.top");Q17=makeQuery(id+"F4.opExtrude","CAP_EDGE",EDGE,{"disambiguationData":[OSD([subQ0]),TDD([makeQuery(id+"F0.imprint","IMPRINT",EDGE,{"disambiguationData":[TD([[makeQuery(id+"F0.imprint","INTERSECT",VERTEX,{"derivedFrom":[subQ0,sQuery(id+"F0.wireOp",EDGE,"E4.left")]}),-1.0]])],"derivedFrom":subQ0})])],"isStart":true});}
            var Q18;
            {var subQ0=sQuery(id+"F0.wireOp",EDGE,"E4.right");Q18=makeQuery(id+"F4.opExtrude","CAP_EDGE",EDGE,{"disambiguationData":[OSD([subQ0]),TDD([makeQuery(id+"F0.imprint","IMPRINT",EDGE,{"disambiguationData":[TD([[makeQuery(id+"F0.imprint","INTERSECT",VERTEX,{"derivedFrom":[sQuery(id+"F0.wireOp",EDGE,"E4.top"),subQ0]}),1.0]])],"derivedFrom":subQ0})])],"isStart":true});}
            var Q19;
            {var subQ0=sQuery(id+"F0.wireOp",EDGE,"E4.top");Q19=makeQuery(id+"F4.opExtrude","CAP_EDGE",EDGE,{"disambiguationData":[OSD([subQ0]),TDD([makeQuery(id+"F0.imprint","IMPRINT",EDGE,{"disambiguationData":[TD([[makeQuery(id+"F0.imprint","INTERSECT",VERTEX,{"derivedFrom":[subQ0,sQuery(id+"F0.wireOp",EDGE,"E4.right")]}),1.0]])],"derivedFrom":subQ0})])],"isStart":true});}
            var Q20;
            {var subQ0=sQuery(id+"F0.wireOp",EDGE,"E4.right");Q20=makeQuery(id+"F4.opExtrude","CAP_EDGE",EDGE,{"disambiguationData":[OSD([subQ0]),TDD([makeQuery(id+"F0.imprint","IMPRINT",EDGE,{"disambiguationData":[TD([[makeQuery(id+"F0.imprint","INTERSECT",VERTEX,{"derivedFrom":[sQuery(id+"F0.wireOp",EDGE,"E4.bottom"),subQ0]}),-1.0]])],"derivedFrom":subQ0})])],"isStart":true});}
            var Q21;
            {var subQ0=sQuery(id+"F0.wireOp",EDGE,"E4.bottom");Q21=makeQuery(id+"F4.opExtrude","CAP_EDGE",EDGE,{"disambiguationData":[OSD([subQ0]),TDD([makeQuery(id+"F0.imprint","IMPRINT",EDGE,{"disambiguationData":[TD([[makeQuery(id+"F0.imprint","INTERSECT",VERTEX,{"derivedFrom":[subQ0,sQuery(id+"F0.wireOp",EDGE,"E4.right")]}),1.0]])],"derivedFrom":subQ0})])],"isStart":true});}
            fillet(context, id + "F13", {"entities" : qUnion([Q0, Q1, Q2, Q3, Q4, Q5, Q6, Q7, Q8, Q9, Q10, Q11, Q12, Q13, Q14, Q15, Q16, Q17, Q18, Q19, Q20, Q21]), "radius" : 5 * mm, "tangentPropagation" : true, "allowEdgeOverflow" : false});
        }
        {
            var Q0;
            Q0=makeQuery(id+"F2.opExtrude","CAP_EDGE",EDGE,{"disambiguationData":[OSD([sQuery(id+"F0.wireOp",EDGE,"E2")])],"isStart":false});
            chamfer(context, id + "F14", {"entities" : qUnion([Q0]), "width" : 2 * mm, "tangentPropagation" : true});
        }
        {
            var Q0;
            Q0=makeQuery(id+"F2.opExtrude","CAP_EDGE",EDGE,{"disambiguationData":[OSD([sQuery(id+"F0.wireOp",EDGE,"E2")])],"isStart":true});
            chamfer(context, id + "F15", {"entities" : qUnion([Q0]), "width" : 4 * mm, "tangentPropagation" : true});
        }
        {
            var Q0;
            Q0=makeQuery(id+"F15.opChamfer","BLEND_EDGE",EDGE,{"blendedFrom":[makeQuery(id+"F2.opExtrude","CAP_EDGE",EDGE,{"disambiguationData":[OSD([sQuery(id+"F0.wireOp",EDGE,"E2")])],"isStart":true}),makeQuery(id+"F3.boolean.opBoolean","COPY",FACE,{"derivedFrom":makeQuery(id+"F3.opExtrude","SWEPT_FACE",FACE,{"disambiguationData":[OSD([sQuery(id+"F0.wireOp",EDGE,"E3.2.0")])]})})],"blendedInto":[makeQuery(id+"F3.boolean.opBoolean","COPY",FACE,{"derivedFrom":makeQuery(id+"F3.opExtrude","SWEPT_FACE",FACE,{"disambiguationData":[OSD([sQuery(id+"F0.wireOp",EDGE,"E3.2.0")])]})})]});
            var Q1;
            Q1=makeQuery(id+"F3.boolean.opBoolean","COPY",EDGE,{"derivedFrom":makeQuery(id+"F3.opExtrude","CAP_EDGE",EDGE,{"disambiguationData":[OSD([sQuery(id+"F0.wireOp",EDGE,"E3.2.0")])],"isStart":true})});
            var Q2;
            Q2=makeQuery(id+"F3.boolean.opBoolean","COPY",EDGE,{"derivedFrom":makeQuery(id+"F3.opExtrude","CAP_EDGE",EDGE,{"disambiguationData":[OSD([sQuery(id+"F0.wireOp",EDGE,"E3.1.0")])],"isStart":true})});
            var Q3;
            Q3=makeQuery(id+"F15.opChamfer","BLEND_EDGE",EDGE,{"blendedFrom":[makeQuery(id+"F2.opExtrude","CAP_EDGE",EDGE,{"disambiguationData":[OSD([sQuery(id+"F0.wireOp",EDGE,"E2")])],"isStart":true}),makeQuery(id+"F3.boolean.opBoolean","COPY",FACE,{"derivedFrom":makeQuery(id+"F3.opExtrude","SWEPT_FACE",FACE,{"disambiguationData":[OSD([sQuery(id+"F0.wireOp",EDGE,"E3.1.0")])]})})],"blendedInto":[makeQuery(id+"F3.boolean.opBoolean","COPY",FACE,{"derivedFrom":makeQuery(id+"F3.opExtrude","SWEPT_FACE",FACE,{"disambiguationData":[OSD([sQuery(id+"F0.wireOp",EDGE,"E3.1.0")])]})})]});
            var Q4;
            Q4=makeQuery(id+"F3.boolean.opBoolean","COPY",EDGE,{"derivedFrom":makeQuery(id+"F3.opExtrude","CAP_EDGE",EDGE,{"disambiguationData":[OSD([sQuery(id+"F0.wireOp",EDGE,"E1")])],"isStart":true})});
            var Q5;
            Q5=makeQuery(id+"F15.opChamfer","BLEND_EDGE",EDGE,{"blendedFrom":[makeQuery(id+"F2.opExtrude","CAP_EDGE",EDGE,{"disambiguationData":[OSD([sQuery(id+"F0.wireOp",EDGE,"E2")])],"isStart":true}),makeQuery(id+"F3.boolean.opBoolean","COPY",FACE,{"derivedFrom":makeQuery(id+"F3.opExtrude","SWEPT_FACE",FACE,{"disambiguationData":[OSD([sQuery(id+"F0.wireOp",EDGE,"E1")])]})})],"blendedInto":[makeQuery(id+"F3.boolean.opBoolean","COPY",FACE,{"derivedFrom":makeQuery(id+"F3.opExtrude","SWEPT_FACE",FACE,{"disambiguationData":[OSD([sQuery(id+"F0.wireOp",EDGE,"E1")])]})})]});
            var Q6;
            Q6=makeQuery(id+"F3.boolean.opBoolean","COPY",EDGE,{"derivedFrom":makeQuery(id+"F3.opExtrude","CAP_EDGE",EDGE,{"disambiguationData":[OSD([sQuery(id+"F0.wireOp",EDGE,"E3.3.0")])],"isStart":true})});
            var Q7;
            Q7=makeQuery(id+"F15.opChamfer","BLEND_EDGE",EDGE,{"blendedFrom":[makeQuery(id+"F2.opExtrude","CAP_EDGE",EDGE,{"disambiguationData":[OSD([sQuery(id+"F0.wireOp",EDGE,"E2")])],"isStart":true}),makeQuery(id+"F3.boolean.opBoolean","COPY",FACE,{"derivedFrom":makeQuery(id+"F3.opExtrude","SWEPT_FACE",FACE,{"disambiguationData":[OSD([sQuery(id+"F0.wireOp",EDGE,"E3.3.0")])]})})],"blendedInto":[makeQuery(id+"F3.boolean.opBoolean","COPY",FACE,{"derivedFrom":makeQuery(id+"F3.opExtrude","SWEPT_FACE",FACE,{"disambiguationData":[OSD([sQuery(id+"F0.wireOp",EDGE,"E3.3.0")])]})})]});
            var Q8;
            {var subQ0=sQuery(id+"F0.wireOp",EDGE,"E2");Q8=makeQuery(id+"F15.opChamfer","BLEND_EDGE",EDGE,{"blendedFrom":[makeQuery(id+"F2.opExtrude","CAP_EDGE",EDGE,{"disambiguationData":[OSD([subQ0])],"isStart":true}),makeQuery(id+"F2.opExtrude","SWEPT_FACE",FACE,{"disambiguationData":[OSD([subQ0])]})],"blendedInto":[makeQuery(id+"F2.opExtrude","SWEPT_FACE",FACE,{"disambiguationData":[OSD([subQ0])]})]});}
            fillet(context, id + "F16", {"entities" : qUnion([Q0, Q1, Q2, Q3, Q4, Q5, Q6, Q7, Q8]), "radius" : 2 * mm, "tangentPropagation" : true, "allowEdgeOverflow" : false});
        }
        {
            var Q0;
            {var subQ0=sQuery(id+"F0.wireOp",EDGE,"E7.bottom");var subQ1=sQuery(id+"F0.wireOp",EDGE,"E6.left");Q0=makeQuery(id+"F11.opFillet","BLEND_EDGE",EDGE,{"disambiguationData":[OD(0.0)],"blendedFrom":[makeQuery(id+"F9.opFillet","BLEND_EDGE",EDGE,{"blendedFrom":[makeQuery(id+"F2.opExtrude","SWEPT_EDGE",EDGE,{"disambiguationData":[OSD([subQ1,subQ0])]}),makeQuery(id+"F4.opExtrude","CAP_FACE",FACE,{"disambiguationData":[OSD([sQuery(id+"F0.wireOp",EDGE,"E4.bottom"),sQuery(id+"F0.wireOp",EDGE,"E4.left"),subQ1,subQ0,sQuery(id+"F0.wireOp",EDGE,"E13"),sQuery(id+"F0.wireOp",EDGE,"E15")])],"isStart":false})],"blendedInto":[makeQuery(id+"F4.opExtrude","CAP_FACE",FACE,{"disambiguationData":[OSD([sQuery(id+"F0.wireOp",EDGE,"E4.bottom"),sQuery(id+"F0.wireOp",EDGE,"E4.left"),subQ1,subQ0,sQuery(id+"F0.wireOp",EDGE,"E13"),sQuery(id+"F0.wireOp",EDGE,"E15")])],"isStart":false})]}),makeQuery(id+"F2.opExtrude","CAP_FACE",FACE,{"disambiguationData":[OSD([sQuery(id+"F0.wireOp",EDGE,"E0"),sQuery(id+"F0.wireOp",EDGE,"E2"),sQuery(id+"F0.wireOp",EDGE,"E3.1.1"),sQuery(id+"F0.wireOp",EDGE,"E3.2.1"),sQuery(id+"F0.wireOp",EDGE,"E3.3.1"),subQ1,sQuery(id+"F0.wireOp",EDGE,"E6.right"),subQ0,sQuery(id+"F0.wireOp",EDGE,"E7.top")])],"isStart":false})],"blendedInto":[makeQuery(id+"F2.opExtrude","CAP_FACE",FACE,{"disambiguationData":[OSD([sQuery(id+"F0.wireOp",EDGE,"E0"),sQuery(id+"F0.wireOp",EDGE,"E2"),sQuery(id+"F0.wireOp",EDGE,"E3.1.1"),sQuery(id+"F0.wireOp",EDGE,"E3.2.1"),sQuery(id+"F0.wireOp",EDGE,"E3.3.1"),subQ1,sQuery(id+"F0.wireOp",EDGE,"E6.right"),subQ0,sQuery(id+"F0.wireOp",EDGE,"E7.top")])],"isStart":false})]});}
            fillet(context, id + "F17", {"entities" : qUnion([Q0]), "radius" : 2 * mm, "tangentPropagation" : true, "allowEdgeOverflow" : false});
        }
    });
